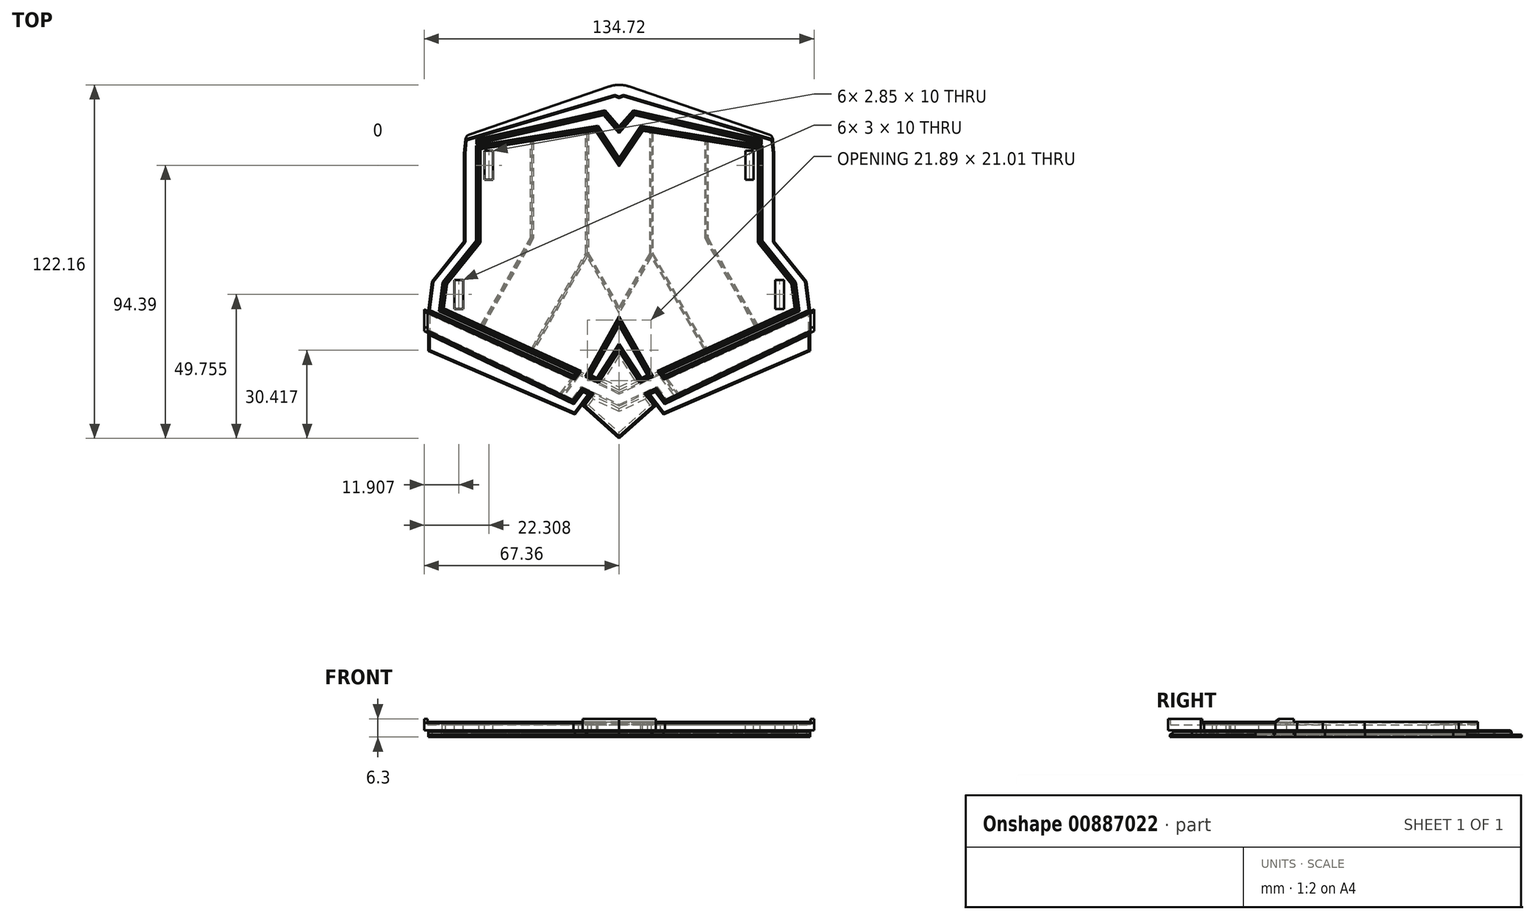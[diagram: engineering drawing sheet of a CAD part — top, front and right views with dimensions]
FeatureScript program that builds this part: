
annotation { "Feature Type Name" : "Feature", "Feature Type Description" : "" }
export const myFeature = defineFeature(function(context is Context, id is Id, definition is map)
    precondition{}
    {
        {
            var Q0;
            Q0=qCreatedBy(makeId("Top.planeOp"),FACE);
            var sketch = newSketch(context, id + "F0", { "sketchPlane" : qUnion([Q0])});
            skLineSegment(sketch, "E0", {"start": v(0, 68.56) * mm, "end": v(1.41, 69.18) * mm});
            skLineSegment(sketch, "E1", {"start": v(1.41, 69.18) * mm, "end": v(53.17, 53.82) * mm});
            skLineSegment(sketch, "E2", {"start": v(53.17, 53.82) * mm, "end": v(53.6, 49) * mm});
            skLineSegment(sketch, "E3", {"start": v(53.6, 49) * mm, "end": v(53.6, 18.48) * mm});
            skLineSegment(sketch, "E4", {"start": v(53.6, 18.48) * mm, "end": v(64.65, 4.74) * mm});
            skLineSegment(sketch, "E5", {"start": v(64.65, 4.74) * mm, "end": v(65.96, -5.54) * mm});
            skLineSegment(sketch, "E6", {"start": v(65.96, -5.54) * mm, "end": v(65.96, -19.34) * mm});
            skLineSegment(sketch, "E7", {"start": v(65.96, -19.34) * mm, "end": v(15.29, -41.25) * mm});
            skLineSegment(sketch, "E8", {"start": v(15.29, -41.25) * mm, "end": v(12.57, -37.67) * mm});
            skLineSegment(sketch, "E9", {"start": v(12.57, -37.67) * mm, "end": v(0, -48.86) * mm});
            skLineSegment(sketch, "E10.MirrorCS", {"start": v(-15.29, -41.25) * mm, "end": v(-12.57, -37.67) * mm});
            skLineSegment(sketch, "E11.MirrorCS", {"start": v(0, 68.56) * mm, "end": v(-1.41, 69.18) * mm});
            skLineSegment(sketch, "E12.MirrorCS", {"start": v(-53.6, 18.48) * mm, "end": v(-64.65, 4.74) * mm});
            skLineSegment(sketch, "E13.MirrorCS", {"start": v(-65.96, -5.54) * mm, "end": v(-65.96, -19.34) * mm});
            skLineSegment(sketch, "E14.MirrorCS", {"start": v(-65.96, -19.34) * mm, "end": v(-15.29, -41.25) * mm});
            skLineSegment(sketch, "E15.MirrorCS", {"start": v(-53.17, 53.82) * mm, "end": v(-53.6, 49) * mm});
            skLineSegment(sketch, "E16.MirrorCS", {"start": v(-1.41, 69.18) * mm, "end": v(-53.17, 53.82) * mm});
            skLineSegment(sketch, "E17.MirrorCS", {"start": v(-53.6, 49) * mm, "end": v(-53.6, 18.48) * mm});
            skLineSegment(sketch, "E18.MirrorCS", {"start": v(-12.57, -37.67) * mm, "end": v(0, -48.86) * mm});
            skLineSegment(sketch, "E19.MirrorCS", {"start": v(-64.65, 4.74) * mm, "end": v(-65.96, -5.54) * mm});
            skLineSegment(sketch, "E20", {"start": v(3.44, 72.1) * mm, "end": v(51.78, 55.53) * mm});
            skArc(sketch, "E21", {"start": v(53.17, 53.82) * mm, "mid": v(52.72, 54.88) * mm, "end": v(51.78, 55.53) * mm});
            skArc(sketch, "E22", {"start": v(3.44, 72.1) * mm, "mid": v(1.75, 72.52) * mm, "end": v(0, 72.62) * mm});
            skArc(sketch, "E23.MirrorCS", {"start": v(-3.44, 72.1) * mm, "mid": v(-1.75, 72.52) * mm, "end": v(0, 72.62) * mm});
            skLineSegment(sketch, "E24.MirrorCS", {"start": v(-3.44, 72.1) * mm, "end": v(-51.78, 55.53) * mm});
            skArc(sketch, "E25.MirrorCS", {"start": v(-53.17, 53.82) * mm, "mid": v(-52.72, 54.88) * mm, "end": v(-51.78, 55.53) * mm});
            skSolve(sketch);
        }
        {
            var Q0;
            Q0 = qSketchRegion(id + "F0", true);
            extrude(context, id + "F1", {"entities" : qUnion([Q0]), "depth" : .8 * mm, "offsetDistance" : 25 * mm});
        }
        {
            var Q0;
            Q0=makeQuery(id+"F1.opExtrude","CAP_FACE",FACE,{"disambiguationData":[OSD([sQuery(id+"F0.wireOp",EDGE,"E2"),sQuery(id+"F0.wireOp",EDGE,"E3"),sQuery(id+"F0.wireOp",EDGE,"E4"),sQuery(id+"F0.wireOp",EDGE,"E5"),sQuery(id+"F0.wireOp",EDGE,"E6"),sQuery(id+"F0.wireOp",EDGE,"E7"),sQuery(id+"F0.wireOp",EDGE,"E8"),sQuery(id+"F0.wireOp",EDGE,"E9"),sQuery(id+"F0.wireOp",EDGE,"E10.MirrorCS"),sQuery(id+"F0.wireOp",EDGE,"E12.MirrorCS"),sQuery(id+"F0.wireOp",EDGE,"E13.MirrorCS"),sQuery(id+"F0.wireOp",EDGE,"E14.MirrorCS"),sQuery(id+"F0.wireOp",EDGE,"E15.MirrorCS"),sQuery(id+"F0.wireOp",EDGE,"E17.MirrorCS"),sQuery(id+"F0.wireOp",EDGE,"E18.MirrorCS"),sQuery(id+"F0.wireOp",EDGE,"E19.MirrorCS"),sQuery(id+"F0.wireOp",EDGE,"E20"),sQuery(id+"F0.wireOp",EDGE,"E21"),sQuery(id+"F0.wireOp",EDGE,"E22"),sQuery(id+"F0.wireOp",EDGE,"E23.MirrorCS"),sQuery(id+"F0.wireOp",EDGE,"E24.MirrorCS"),sQuery(id+"F0.wireOp",EDGE,"E25.MirrorCS")])],"isStart":false});
            var sketch = newSketch(context, id + "F2", { "sketchPlane" : qUnion([Q0])});
            skLineSegment(sketch, "E26", {"start": v(48.77, 53.39) * mm, "end": v(48.77, 18.48) * mm});
            skLineSegment(sketch, "E27", {"start": v(48.77, 18.48) * mm, "end": v(60.35, 4.1) * mm});
            skLineSegment(sketch, "E28", {"start": v(60.35, 4.1) * mm, "end": v(61.53, -5.14) * mm});
            skLineSegment(sketch, "E29", {"start": v(61.53, -5.14) * mm, "end": v(14.26, -26.68) * mm});
            skLineSegment(sketch, "E30", {"start": v(65.96, -5.54) * mm, "end": v(15.61, -28.48) * mm});
            skLineSegment(sketch, "E31", {"start": v(15.61, -28.48) * mm, "end": v(14.26, -26.68) * mm});
            skLineSegment(sketch, "E32", {"start": v(53.6, 49) * mm, "end": v(53.17, 53.82) * mm});
            skLineSegment(sketch, "E33", {"start": v(53.17, 53.82) * mm, "end": v(1.41, 69.18) * mm});
            skLineSegment(sketch, "E34", {"start": v(1.41, 69.18) * mm, "end": v(0, 68.56) * mm});
            skLineSegment(sketch, "E35", {"start": v(0, 57.52) * mm, "end": v(5.09, 63.36) * mm});
            skLineSegment(sketch, "E36", {"start": v(5.09, 63.36) * mm, "end": v(48.77, 53.39) * mm});
            skLineSegment(sketch, "E37", {"start": v(53.6, 49) * mm, "end": v(53.6, 18.48) * mm});
            skLineSegment(sketch, "E38", {"start": v(53.6, 18.48) * mm, "end": v(64.65, 4.74) * mm});
            skLineSegment(sketch, "E39", {"start": v(64.65, 4.74) * mm, "end": v(65.96, -5.54) * mm});
            skLineSegment(sketch, "E40.MirrorCS", {"start": v(-15.61, -28.48) * mm, "end": v(-14.26, -26.68) * mm});
            skLineSegment(sketch, "E41.MirrorCS", {"start": v(-1.41, 69.18) * mm, "end": v(0, 68.56) * mm});
            skLineSegment(sketch, "E42.MirrorCS", {"start": v(-60.35, 4.1) * mm, "end": v(-61.53, -5.14) * mm});
            skLineSegment(sketch, "E43.MirrorCS", {"start": v(-61.53, -5.14) * mm, "end": v(-14.26, -26.68) * mm});
            skLineSegment(sketch, "E44.MirrorCS", {"start": v(-64.65, 4.74) * mm, "end": v(-65.96, -5.54) * mm});
            skLineSegment(sketch, "E45.MirrorCS", {"start": v(-53.6, 49) * mm, "end": v(-53.17, 53.82) * mm});
            skLineSegment(sketch, "E46.MirrorCS", {"start": v(0, 57.52) * mm, "end": v(-5.09, 63.36) * mm});
            skLineSegment(sketch, "E47.MirrorCS", {"start": v(-53.6, 18.48) * mm, "end": v(-64.65, 4.74) * mm});
            skLineSegment(sketch, "E48.MirrorCS", {"start": v(-48.77, 53.39) * mm, "end": v(-48.77, 18.48) * mm});
            skLineSegment(sketch, "E49.MirrorCS", {"start": v(-53.6, 49) * mm, "end": v(-53.6, 18.48) * mm});
            skLineSegment(sketch, "E50.MirrorCS", {"start": v(-53.17, 53.82) * mm, "end": v(-1.41, 69.18) * mm});
            skLineSegment(sketch, "E51.MirrorCS", {"start": v(-5.09, 63.36) * mm, "end": v(-48.77, 53.39) * mm});
            skLineSegment(sketch, "E52.MirrorCS", {"start": v(-65.96, -5.54) * mm, "end": v(-15.61, -28.48) * mm});
            skLineSegment(sketch, "E53.MirrorCS", {"start": v(-48.77, 18.48) * mm, "end": v(-60.35, 4.1) * mm});
            skSolve(sketch);
        }
        {
            var Q0;
            Q0=qSketchRegion(id+"F2",true);
            extrude(context, id + "F3", {"entities" : qUnion([Q0]), "operationType" : NewBodyOperationType.ADD, "depth" : 1.5 * mm, "offsetDistance" : 25 * mm});
        }
        {
            var Q0;
            {var subQ0=sQuery(id+"F0.wireOp",EDGE,"E8");var subQ1=sQuery(id+"F0.wireOp",EDGE,"E7");var subQ2=sQuery(id+"F0.wireOp",EDGE,"E6");var subQ3=sQuery(id+"F0.wireOp",EDGE,"E19.MirrorCS");var subQ4=sQuery(id+"F0.wireOp",EDGE,"E5");var subQ5=sQuery(id+"F0.wireOp",EDGE,"E18.MirrorCS");var subQ6=sQuery(id+"F0.wireOp",EDGE,"E9");var subQ7=sQuery(id+"F0.wireOp",EDGE,"E10.MirrorCS");var subQ8=sQuery(id+"F0.wireOp",EDGE,"E13.MirrorCS");var subQ9=sQuery(id+"F0.wireOp",EDGE,"E14.MirrorCS");Q0=makeQuery(id+"F3.boolean.opBoolean","SPLIT",FACE,{"disambiguationData":[TD([makeQuery(id+"F1.opExtrude","SWEPT_FACE",FACE,{"disambiguationData":[OSD([subQ4])]})])],"derivedFrom":makeQuery(id+"F1.opExtrude","CAP_FACE",FACE,{"disambiguationData":[OSD([sQuery(id+"F0.wireOp",EDGE,"E2"),sQuery(id+"F0.wireOp",EDGE,"E3"),sQuery(id+"F0.wireOp",EDGE,"E4"),subQ4,subQ2,subQ1,subQ0,subQ6,subQ7,sQuery(id+"F0.wireOp",EDGE,"E12.MirrorCS"),subQ8,subQ9,sQuery(id+"F0.wireOp",EDGE,"E15.MirrorCS"),sQuery(id+"F0.wireOp",EDGE,"E17.MirrorCS"),subQ5,subQ3,sQuery(id+"F0.wireOp",EDGE,"E20"),sQuery(id+"F0.wireOp",EDGE,"E21"),sQuery(id+"F0.wireOp",EDGE,"E22"),sQuery(id+"F0.wireOp",EDGE,"E23.MirrorCS"),sQuery(id+"F0.wireOp",EDGE,"E24.MirrorCS"),sQuery(id+"F0.wireOp",EDGE,"E25.MirrorCS")])],"isStart":false})});}
            var sketch = newSketch(context, id + "F4", { "sketchPlane" : qUnion([Q0])});
            skLineSegment(sketch, "E54", {"start": v(0, 56.8) * mm, "end": v(5.24, 62.81) * mm});
            skLineSegment(sketch, "E55", {"start": v(5.24, 62.81) * mm, "end": v(48.77, 52.87) * mm});
            skLineSegment(sketch, "E56", {"start": v(48.77, 52.87) * mm, "end": v(48.77, 51.1) * mm});
            skLineSegment(sketch, "E57", {"start": v(48.77, 51.1) * mm, "end": v(7.78, 57.76) * mm});
            skLineSegment(sketch, "E58", {"start": v(7.78, 57.76) * mm, "end": v(0, 46.14) * mm});
            skLineSegment(sketch, "E59.MirrorCS", {"start": v(-48.77, 52.87) * mm, "end": v(-48.77, 51.1) * mm});
            skLineSegment(sketch, "E60.MirrorCS", {"start": v(-48.77, 51.1) * mm, "end": v(-7.78, 57.76) * mm});
            skLineSegment(sketch, "E61.MirrorCS", {"start": v(-5.24, 62.81) * mm, "end": v(-48.77, 52.87) * mm});
            skLineSegment(sketch, "E62.MirrorCS", {"start": v(0, 56.8) * mm, "end": v(-5.24, 62.81) * mm});
            skLineSegment(sketch, "E63.MirrorCS", {"start": v(-7.78, 57.76) * mm, "end": v(0, 46.14) * mm});
            skSolve(sketch);
        }
        {
            var Q0;
            Q0=qSketchRegion(id+"F4",true);
            extrude(context, id + "F5", {"entities" : qUnion([Q0]), "operationType" : NewBodyOperationType.ADD, "depth" : 1.5 * mm, "offsetDistance" : 25 * mm});
        }
        {
            var Q0;
            {var subQ7=sQuery(id+"F0.wireOp",EDGE,"E8");var subQ9=sQuery(id+"F0.wireOp",EDGE,"E7");var subQ11=sQuery(id+"F0.wireOp",EDGE,"E6");var subQ14=sQuery(id+"F0.wireOp",EDGE,"E19.MirrorCS");var subQ16=sQuery(id+"F0.wireOp",EDGE,"E5");var subQ17=makeQuery(id+"F1.opExtrude","SWEPT_FACE",FACE,{"disambiguationData":[OSD([subQ16])]});var subQ19=sQuery(id+"F0.wireOp",EDGE,"E18.MirrorCS");var subQ22=sQuery(id+"F0.wireOp",EDGE,"E9");var subQ24=sQuery(id+"F0.wireOp",EDGE,"E10.MirrorCS");var subQ27=sQuery(id+"F0.wireOp",EDGE,"E13.MirrorCS");var subQ30=sQuery(id+"F0.wireOp",EDGE,"E14.MirrorCS");Q0=makeQuery(id+"F5.boolean.opBoolean","SPLIT",FACE,{"disambiguationData":[TD([subQ17])],"derivedFrom":makeQuery(id+"F3.boolean.opBoolean","SPLIT",FACE,{"disambiguationData":[TD([subQ17])],"derivedFrom":makeQuery(id+"F1.opExtrude","CAP_FACE",FACE,{"disambiguationData":[OSD([sQuery(id+"F0.wireOp",EDGE,"E2"),sQuery(id+"F0.wireOp",EDGE,"E3"),sQuery(id+"F0.wireOp",EDGE,"E4"),subQ16,subQ11,subQ9,subQ7,subQ22,subQ24,sQuery(id+"F0.wireOp",EDGE,"E12.MirrorCS"),subQ27,subQ30,sQuery(id+"F0.wireOp",EDGE,"E15.MirrorCS"),sQuery(id+"F0.wireOp",EDGE,"E17.MirrorCS"),subQ19,subQ14,sQuery(id+"F0.wireOp",EDGE,"E20"),sQuery(id+"F0.wireOp",EDGE,"E21"),sQuery(id+"F0.wireOp",EDGE,"E22"),sQuery(id+"F0.wireOp",EDGE,"E23.MirrorCS"),sQuery(id+"F0.wireOp",EDGE,"E24.MirrorCS"),sQuery(id+"F0.wireOp",EDGE,"E25.MirrorCS")])],"isStart":false})})});}
            var sketch = newSketch(context, id + "F6", { "sketchPlane" : qUnion([Q0])});
            skLineSegment(sketch, "E64", {"start": v(0, -9.12) * mm, "end": v(10.6, -27.8) * mm});
            skLineSegment(sketch, "E65", {"start": v(10.6, -27.8) * mm, "end": v(7.46, -29.31) * mm});
            skLineSegment(sketch, "E66", {"start": v(7.46, -29.31) * mm, "end": v(0, -17.78) * mm});
            skLineSegment(sketch, "E67", {"start": v(12.66, -32.86) * mm, "end": v(9.9, -34.17) * mm});
            skLineSegment(sketch, "E68", {"start": v(9.9, -34.17) * mm, "end": v(15.28, -41.22) * mm});
            skLineSegment(sketch, "E69", {"start": v(15.28, -41.22) * mm, "end": v(65.96, -19.32) * mm});
            skLineSegment(sketch, "E70", {"start": v(65.96, -19.32) * mm, "end": v(65.96, -13.1) * mm});
            skLineSegment(sketch, "E71", {"start": v(65.96, -13.1) * mm, "end": v(15.81, -37.08) * mm});
            skLineSegment(sketch, "E72", {"start": v(15.81, -37.08) * mm, "end": v(12.66, -32.86) * mm});
            skLineSegment(sketch, "E73.MirrorCS", {"start": v(-12.66, -32.86) * mm, "end": v(-9.9, -34.17) * mm});
            skLineSegment(sketch, "E74.MirrorCS", {"start": v(-15.81, -37.08) * mm, "end": v(-12.66, -32.86) * mm});
            skLineSegment(sketch, "E75.MirrorCS", {"start": v(-10.6, -27.8) * mm, "end": v(-7.46, -29.31) * mm});
            skLineSegment(sketch, "E76.MirrorCS", {"start": v(-65.96, -19.32) * mm, "end": v(-65.96, -13.1) * mm});
            skLineSegment(sketch, "E77.MirrorCS", {"start": v(-65.96, -13.1) * mm, "end": v(-15.81, -37.08) * mm});
            skLineSegment(sketch, "E78.MirrorCS", {"start": v(-9.9, -34.17) * mm, "end": v(-15.28, -41.22) * mm});
            skLineSegment(sketch, "E79.MirrorCS", {"start": v(-15.28, -41.22) * mm, "end": v(-65.96, -19.32) * mm});
            skLineSegment(sketch, "E80.MirrorCS", {"start": v(-7.46, -29.31) * mm, "end": v(0, -17.78) * mm});
            skLineSegment(sketch, "E81.MirrorCS", {"start": v(0, -9.12) * mm, "end": v(-10.6, -27.8) * mm});
            skSolve(sketch);
        }
        {
            var Q0;
            Q0=qSketchRegion(id+"F6",true);
            extrude(context, id + "F7", {"entities" : qUnion([Q0]), "operationType" : NewBodyOperationType.ADD, "depth" : 1.5 * mm, "offsetDistance" : 25 * mm});
        }
        {
            var Q0;
            {var subQ7=sQuery(id+"F0.wireOp",EDGE,"E8");var subQ9=sQuery(id+"F0.wireOp",EDGE,"E7");var subQ11=sQuery(id+"F0.wireOp",EDGE,"E6");var subQ14=sQuery(id+"F0.wireOp",EDGE,"E19.MirrorCS");var subQ16=sQuery(id+"F0.wireOp",EDGE,"E5");var subQ17=makeQuery(id+"F1.opExtrude","SWEPT_FACE",FACE,{"disambiguationData":[OSD([subQ16])]});var subQ19=sQuery(id+"F0.wireOp",EDGE,"E18.MirrorCS");var subQ22=sQuery(id+"F0.wireOp",EDGE,"E9");var subQ24=sQuery(id+"F0.wireOp",EDGE,"E10.MirrorCS");var subQ27=sQuery(id+"F0.wireOp",EDGE,"E13.MirrorCS");var subQ30=sQuery(id+"F0.wireOp",EDGE,"E14.MirrorCS");Q0=makeQuery(id+"F5.boolean.opBoolean","SPLIT",FACE,{"disambiguationData":[TD([subQ17])],"derivedFrom":makeQuery(id+"F3.boolean.opBoolean","SPLIT",FACE,{"disambiguationData":[TD([subQ17])],"derivedFrom":makeQuery(id+"F1.opExtrude","CAP_FACE",FACE,{"disambiguationData":[OSD([sQuery(id+"F0.wireOp",EDGE,"E2"),sQuery(id+"F0.wireOp",EDGE,"E3"),sQuery(id+"F0.wireOp",EDGE,"E4"),subQ16,subQ11,subQ9,subQ7,subQ22,subQ24,sQuery(id+"F0.wireOp",EDGE,"E12.MirrorCS"),subQ27,subQ30,sQuery(id+"F0.wireOp",EDGE,"E15.MirrorCS"),sQuery(id+"F0.wireOp",EDGE,"E17.MirrorCS"),subQ19,subQ14,sQuery(id+"F0.wireOp",EDGE,"E20"),sQuery(id+"F0.wireOp",EDGE,"E21"),sQuery(id+"F0.wireOp",EDGE,"E22"),sQuery(id+"F0.wireOp",EDGE,"E23.MirrorCS"),sQuery(id+"F0.wireOp",EDGE,"E24.MirrorCS"),sQuery(id+"F0.wireOp",EDGE,"E25.MirrorCS")])],"isStart":false})})});}
            var sketch = newSketch(context, id + "F8", { "sketchPlane" : qUnion([Q0])});
            skLineSegment(sketch, "E82", {"start": v(65.96, -6.1) * mm, "end": v(15.92, -28.9) * mm});
            skLineSegment(sketch, "E83", {"start": v(15.92, -28.9) * mm, "end": v(20.1, -34.47) * mm});
            skLineSegment(sketch, "E84", {"start": v(20.1, -34.47) * mm, "end": v(65.96, -12.55) * mm});
            skLineSegment(sketch, "E85", {"start": v(65.96, -12.55) * mm, "end": v(65.96, -6.1) * mm});
            skLineSegment(sketch, "E86.MirrorCS", {"start": v(-15.92, -28.9) * mm, "end": v(-20.1, -34.47) * mm});
            skLineSegment(sketch, "E87.MirrorCS", {"start": v(-65.96, -12.55) * mm, "end": v(-65.96, -6.1) * mm});
            skLineSegment(sketch, "E88.MirrorCS", {"start": v(-65.96, -6.1) * mm, "end": v(-15.92, -28.9) * mm});
            skLineSegment(sketch, "E89.MirrorCS", {"start": v(-20.1, -34.47) * mm, "end": v(-65.96, -12.55) * mm});
            skSolve(sketch);
        }
        {
            var Q0;
            Q0=qSketchRegion(id+"F8",true);
            extrude(context, id + "F9", {"entities" : qUnion([Q0]), "operationType" : NewBodyOperationType.ADD, "depth" : 1.5 * mm, "offsetDistance" : 25 * mm});
        }
        {
            var Q0;
            {var subQ7=sQuery(id+"F0.wireOp",EDGE,"E8");var subQ9=sQuery(id+"F0.wireOp",EDGE,"E7");var subQ11=sQuery(id+"F0.wireOp",EDGE,"E6");var subQ14=sQuery(id+"F0.wireOp",EDGE,"E19.MirrorCS");var subQ16=sQuery(id+"F0.wireOp",EDGE,"E5");var subQ17=makeQuery(id+"F1.opExtrude","SWEPT_FACE",FACE,{"disambiguationData":[OSD([subQ16])]});var subQ19=sQuery(id+"F0.wireOp",EDGE,"E18.MirrorCS");var subQ22=sQuery(id+"F0.wireOp",EDGE,"E9");var subQ24=sQuery(id+"F0.wireOp",EDGE,"E10.MirrorCS");var subQ27=sQuery(id+"F0.wireOp",EDGE,"E13.MirrorCS");var subQ30=sQuery(id+"F0.wireOp",EDGE,"E14.MirrorCS");Q0=makeQuery(id+"F5.boolean.opBoolean","SPLIT",FACE,{"disambiguationData":[TD([subQ17])],"derivedFrom":makeQuery(id+"F3.boolean.opBoolean","SPLIT",FACE,{"disambiguationData":[TD([subQ17])],"derivedFrom":makeQuery(id+"F1.opExtrude","CAP_FACE",FACE,{"disambiguationData":[OSD([sQuery(id+"F0.wireOp",EDGE,"E2"),sQuery(id+"F0.wireOp",EDGE,"E3"),sQuery(id+"F0.wireOp",EDGE,"E4"),subQ16,subQ11,subQ9,subQ7,subQ22,subQ24,sQuery(id+"F0.wireOp",EDGE,"E12.MirrorCS"),subQ27,subQ30,sQuery(id+"F0.wireOp",EDGE,"E15.MirrorCS"),sQuery(id+"F0.wireOp",EDGE,"E17.MirrorCS"),subQ19,subQ14,sQuery(id+"F0.wireOp",EDGE,"E20"),sQuery(id+"F0.wireOp",EDGE,"E21"),sQuery(id+"F0.wireOp",EDGE,"E22"),sQuery(id+"F0.wireOp",EDGE,"E23.MirrorCS"),sQuery(id+"F0.wireOp",EDGE,"E24.MirrorCS"),sQuery(id+"F0.wireOp",EDGE,"E25.MirrorCS")])],"isStart":false})})});}
            var sketch = newSketch(context, id + "F10", { "sketchPlane" : qUnion([Q0])});
            skLineSegment(sketch, "E90", {"start": v(0, -38.38) * mm, "end": v(12.83, -32.26) * mm});
            skLineSegment(sketch, "E91", {"start": v(0, -33.68) * mm, "end": v(13.91, -27.04) * mm});
            skLineSegment(sketch, "E92", {"start": v(13.91, -27.04) * mm, "end": v(19.6, -34.65) * mm});
            skLineSegment(sketch, "E93", {"start": v(12.83, -32.26) * mm, "end": v(16.08, -36.6) * mm});
            skLineSegment(sketch, "E94", {"start": v(16.08, -36.6) * mm, "end": v(19.6, -34.65) * mm});
            skLineSegment(sketch, "E95.MirrorCS", {"start": v(-12.83, -32.26) * mm, "end": v(-16.08, -36.6) * mm});
            skLineSegment(sketch, "E96.MirrorCS", {"start": v(-16.08, -36.6) * mm, "end": v(-19.6, -34.65) * mm});
            skLineSegment(sketch, "E97.MirrorCS", {"start": v(0, -33.68) * mm, "end": v(-13.91, -27.04) * mm});
            skLineSegment(sketch, "E98.MirrorCS", {"start": v(-13.91, -27.04) * mm, "end": v(-19.6, -34.65) * mm});
            skLineSegment(sketch, "E99.MirrorCS", {"start": v(0, -38.38) * mm, "end": v(-12.83, -32.26) * mm});
            skSolve(sketch);
        }
        {
            var Q0;
            Q0=qSketchRegion(id+"F10",true);
            extrude(context, id + "F11", {"entities" : qUnion([Q0]), "operationType" : NewBodyOperationType.ADD, "depth" : 1.5 * mm, "offsetDistance" : 25 * mm});
        }
        {
            var Q0;
            {var subQ7=sQuery(id+"F0.wireOp",EDGE,"E8");var subQ9=sQuery(id+"F0.wireOp",EDGE,"E7");var subQ11=sQuery(id+"F0.wireOp",EDGE,"E6");var subQ14=sQuery(id+"F0.wireOp",EDGE,"E19.MirrorCS");var subQ16=sQuery(id+"F0.wireOp",EDGE,"E5");var subQ17=makeQuery(id+"F1.opExtrude","SWEPT_FACE",FACE,{"disambiguationData":[OSD([subQ16])]});var subQ19=sQuery(id+"F0.wireOp",EDGE,"E18.MirrorCS");var subQ22=sQuery(id+"F0.wireOp",EDGE,"E9");var subQ24=sQuery(id+"F0.wireOp",EDGE,"E10.MirrorCS");var subQ27=sQuery(id+"F0.wireOp",EDGE,"E13.MirrorCS");var subQ30=sQuery(id+"F0.wireOp",EDGE,"E14.MirrorCS");Q0=makeQuery(id+"F5.boolean.opBoolean","SPLIT",FACE,{"disambiguationData":[TD([subQ17])],"derivedFrom":makeQuery(id+"F3.boolean.opBoolean","SPLIT",FACE,{"disambiguationData":[TD([subQ17])],"derivedFrom":makeQuery(id+"F1.opExtrude","CAP_FACE",FACE,{"disambiguationData":[OSD([sQuery(id+"F0.wireOp",EDGE,"E2"),sQuery(id+"F0.wireOp",EDGE,"E3"),sQuery(id+"F0.wireOp",EDGE,"E4"),subQ16,subQ11,subQ9,subQ7,subQ22,subQ24,sQuery(id+"F0.wireOp",EDGE,"E12.MirrorCS"),subQ27,subQ30,sQuery(id+"F0.wireOp",EDGE,"E15.MirrorCS"),sQuery(id+"F0.wireOp",EDGE,"E17.MirrorCS"),subQ19,subQ14,sQuery(id+"F0.wireOp",EDGE,"E20"),sQuery(id+"F0.wireOp",EDGE,"E21"),sQuery(id+"F0.wireOp",EDGE,"E22"),sQuery(id+"F0.wireOp",EDGE,"E23.MirrorCS"),sQuery(id+"F0.wireOp",EDGE,"E24.MirrorCS"),sQuery(id+"F0.wireOp",EDGE,"E25.MirrorCS")])],"isStart":false})})});}
            var sketch = newSketch(context, id + "F12", { "sketchPlane" : qUnion([Q0])});
            skLineSegment(sketch, "E100", {"start": v(0, -32.85) * mm, "end": v(6.76, -29.62) * mm});
            skLineSegment(sketch, "E101", {"start": v(6.76, -29.62) * mm, "end": v(0, -19.16) * mm});
            skLineSegment(sketch, "E102", {"start": v(0, -39.2) * mm, "end": v(9.4, -34.73) * mm});
            skLineSegment(sketch, "E103", {"start": v(9.4, -34.73) * mm, "end": v(12.01, -38.16) * mm});
            skLineSegment(sketch, "E104", {"start": v(12.01, -38.16) * mm, "end": v(0, -48.86) * mm});
            skLineSegment(sketch, "E105.MirrorCS", {"start": v(-12.01, -38.16) * mm, "end": v(0, -48.86) * mm});
            skLineSegment(sketch, "E106.MirrorCS", {"start": v(-9.4, -34.73) * mm, "end": v(-12.01, -38.16) * mm});
            skLineSegment(sketch, "E107.MirrorCS", {"start": v(-6.76, -29.62) * mm, "end": v(0, -19.16) * mm});
            skLineSegment(sketch, "E108.MirrorCS", {"start": v(0, -39.2) * mm, "end": v(-9.4, -34.73) * mm});
            skLineSegment(sketch, "E109.MirrorCS", {"start": v(0, -32.85) * mm, "end": v(-6.76, -29.62) * mm});
            skSolve(sketch);
        }
        {
            var Q0;
            Q0=qSketchRegion(id+"F12",true);
            extrude(context, id + "F13", {"entities" : qUnion([Q0]), "operationType" : NewBodyOperationType.ADD, "depth" : 1 * mm, "offsetDistance" : 25 * mm});
        }
        {
            var Q0;
            Q0=makeQuery(id+"F11.opExtrude","CAP_FACE",FACE,{"disambiguationData":[OSD([sQuery(id+"F10.wireOp",EDGE,"E90"),sQuery(id+"F10.wireOp",EDGE,"E91"),sQuery(id+"F10.wireOp",EDGE,"E92"),sQuery(id+"F10.wireOp",EDGE,"E93"),sQuery(id+"F10.wireOp",EDGE,"E94"),sQuery(id+"F10.wireOp",EDGE,"E95.MirrorCS"),sQuery(id+"F10.wireOp",EDGE,"E96.MirrorCS"),sQuery(id+"F10.wireOp",EDGE,"E97.MirrorCS"),sQuery(id+"F10.wireOp",EDGE,"E98.MirrorCS"),sQuery(id+"F10.wireOp",EDGE,"E99.MirrorCS")])],"isStart":false});
            var sketch = newSketch(context, id + "F14", { "sketchPlane" : qUnion([Q0])});
            skLineSegment(sketch, "E110", {"start": v(67.36, -4.9) * mm, "end": v(67.36, -12.43) * mm});
            skLineSegment(sketch, "E111", {"start": v(12.69, -38.23) * mm, "end": v(0, -49.53) * mm});
            skLineSegment(sketch, "E112", {"start": v(12.69, -38.23) * mm, "end": v(9.7, -34.3) * mm});
            skLineSegment(sketch, "E113", {"start": v(9.7, -34.3) * mm, "end": v(12.68, -32.89) * mm});
            skLineSegment(sketch, "E114", {"start": v(12.68, -32.89) * mm, "end": v(15.81, -37.08) * mm});
            skLineSegment(sketch, "E115", {"start": v(0, -18.24) * mm, "end": v(7.36, -29.62) * mm});
            skLineSegment(sketch, "E116", {"start": v(7.36, -29.62) * mm, "end": v(14.07, -26.42) * mm});
            skLineSegment(sketch, "E117", {"start": v(14.07, -26.42) * mm, "end": v(15.61, -28.48) * mm});
            skLineSegment(sketch, "E118", {"start": v(15.61, -28.48) * mm, "end": v(67.36, -4.9) * mm});
            skLineSegment(sketch, "E119", {"start": v(15.81, -37.08) * mm, "end": v(67.36, -12.43) * mm});
            skLineSegment(sketch, "E120", {"start": v(14.1, -26.48) * mm, "end": v(61.26, -5) * mm});
            skLineSegment(sketch, "E121", {"start": v(61.26, -5) * mm, "end": v(60.1, 4) * mm});
            skLineSegment(sketch, "E122", {"start": v(60.1, 4) * mm, "end": v(48.52, 18.4) * mm});
            skLineSegment(sketch, "E123", {"start": v(48.52, 18.4) * mm, "end": v(48.52, 50.9) * mm});
            skLineSegment(sketch, "E124", {"start": v(48.52, 50.9) * mm, "end": v(7.9, 57.48) * mm});
            skLineSegment(sketch, "E125", {"start": v(7.9, 57.48) * mm, "end": v(0, 45.69) * mm});
            skLineSegment(sketch, "E126", {"start": v(10.95, -27.9) * mm, "end": v(0, -8.6) * mm});
            skLineSegment(sketch, "E127.MirrorCS", {"start": v(-9.7, -34.3) * mm, "end": v(-12.68, -32.89) * mm});
            skLineSegment(sketch, "E128.MirrorCS", {"start": v(-12.69, -38.23) * mm, "end": v(-9.7, -34.3) * mm});
            skLineSegment(sketch, "E129.MirrorCS", {"start": v(-12.68, -32.89) * mm, "end": v(-15.81, -37.08) * mm});
            skLineSegment(sketch, "E130.MirrorCS", {"start": v(-14.07, -26.42) * mm, "end": v(-15.61, -28.48) * mm});
            skLineSegment(sketch, "E131.MirrorCS", {"start": v(-67.36, -4.9) * mm, "end": v(-67.36, -12.43) * mm});
            skLineSegment(sketch, "E132.MirrorCS", {"start": v(-7.36, -29.62) * mm, "end": v(-14.07, -26.42) * mm});
            skLineSegment(sketch, "E133.MirrorCS", {"start": v(-14.1, -26.48) * mm, "end": v(-61.26, -5) * mm});
            skLineSegment(sketch, "E134.MirrorCS", {"start": v(-12.69, -38.23) * mm, "end": v(0, -49.53) * mm});
            skLineSegment(sketch, "E135.MirrorCS", {"start": v(-48.52, 18.4) * mm, "end": v(-48.52, 50.9) * mm});
            skLineSegment(sketch, "E136.MirrorCS", {"start": v(-60.1, 4) * mm, "end": v(-48.52, 18.4) * mm});
            skLineSegment(sketch, "E137.MirrorCS", {"start": v(-10.95, -27.9) * mm, "end": v(0, -8.6) * mm});
            skLineSegment(sketch, "E138.MirrorCS", {"start": v(-48.52, 50.9) * mm, "end": v(-7.9, 57.48) * mm});
            skLineSegment(sketch, "E139.MirrorCS", {"start": v(-15.81, -37.08) * mm, "end": v(-67.36, -12.43) * mm});
            skLineSegment(sketch, "E140.MirrorCS", {"start": v(-15.61, -28.48) * mm, "end": v(-67.36, -4.9) * mm});
            skLineSegment(sketch, "E141.MirrorCS", {"start": v(0, -18.24) * mm, "end": v(-7.36, -29.62) * mm});
            skLineSegment(sketch, "E142.MirrorCS", {"start": v(-61.26, -5) * mm, "end": v(-60.1, 4) * mm});
            skLineSegment(sketch, "E143.MirrorCS", {"start": v(-7.9, 57.48) * mm, "end": v(0, 45.69) * mm});
            skSolve(sketch);
        }
        {
            var Q0;
            Q0 = qSketchRegion(id + "F14", true);
            extrude(context, id + "F15", {"entities" : qUnion([Q0]), "depth" : 2 * mm, "offsetDistance" : 25 * mm});
        }
        {
            var Q0;
            Q0=makeQuery(id+"F1.opExtrude","CAP_FACE",FACE,{"disambiguationData":[OSD([sQuery(id+"F0.wireOp",EDGE,"E2"),sQuery(id+"F0.wireOp",EDGE,"E3"),sQuery(id+"F0.wireOp",EDGE,"E4"),sQuery(id+"F0.wireOp",EDGE,"E5"),sQuery(id+"F0.wireOp",EDGE,"E6"),sQuery(id+"F0.wireOp",EDGE,"E7"),sQuery(id+"F0.wireOp",EDGE,"E8"),sQuery(id+"F0.wireOp",EDGE,"E9"),sQuery(id+"F0.wireOp",EDGE,"E10.MirrorCS"),sQuery(id+"F0.wireOp",EDGE,"E12.MirrorCS"),sQuery(id+"F0.wireOp",EDGE,"E13.MirrorCS"),sQuery(id+"F0.wireOp",EDGE,"E14.MirrorCS"),sQuery(id+"F0.wireOp",EDGE,"E15.MirrorCS"),sQuery(id+"F0.wireOp",EDGE,"E17.MirrorCS"),sQuery(id+"F0.wireOp",EDGE,"E18.MirrorCS"),sQuery(id+"F0.wireOp",EDGE,"E19.MirrorCS"),sQuery(id+"F0.wireOp",EDGE,"E20"),sQuery(id+"F0.wireOp",EDGE,"E21"),sQuery(id+"F0.wireOp",EDGE,"E22"),sQuery(id+"F0.wireOp",EDGE,"E23.MirrorCS"),sQuery(id+"F0.wireOp",EDGE,"E24.MirrorCS"),sQuery(id+"F0.wireOp",EDGE,"E25.MirrorCS")])],"isStart":false});
            var sketch = newSketch(context, id + "F16", { "sketchPlane" : qUnion([Q0])});
            skLineSegment(sketch, "E144", {"start": v(0, 45.24) * mm, "end": v(8.02, 57.21) * mm});
            skLineSegment(sketch, "E145", {"start": v(8.02, 57.21) * mm, "end": v(48.27, 50.68) * mm});
            skLineSegment(sketch, "E146", {"start": v(48.27, 50.68) * mm, "end": v(48.27, 18.3) * mm});
            skLineSegment(sketch, "E147", {"start": v(48.27, 18.3) * mm, "end": v(59.87, 3.9) * mm});
            skLineSegment(sketch, "E148", {"start": v(59.87, 3.9) * mm, "end": v(60.99, -4.84) * mm});
            skLineSegment(sketch, "E149", {"start": v(60.99, -4.84) * mm, "end": v(11.05, -27.59) * mm});
            skLineSegment(sketch, "E150", {"start": v(11.05, -27.59) * mm, "end": v(0, -8.1) * mm});
            skLineSegment(sketch, "E151.MirrorCS", {"start": v(-8.02, 57.21) * mm, "end": v(-48.27, 50.68) * mm});
            skLineSegment(sketch, "E152.MirrorCS", {"start": v(-60.99, -4.84) * mm, "end": v(-11.05, -27.59) * mm});
            skLineSegment(sketch, "E153.MirrorCS", {"start": v(-48.27, 50.68) * mm, "end": v(-48.27, 18.3) * mm});
            skLineSegment(sketch, "E154.MirrorCS", {"start": v(-11.05, -27.59) * mm, "end": v(0, -8.1) * mm});
            skLineSegment(sketch, "E155.MirrorCS", {"start": v(0, 45.24) * mm, "end": v(-8.02, 57.21) * mm});
            skLineSegment(sketch, "E156.MirrorCS", {"start": v(-59.87, 3.9) * mm, "end": v(-60.99, -4.84) * mm});
            skLineSegment(sketch, "E157.MirrorCS", {"start": v(-48.27, 18.3) * mm, "end": v(-59.87, 3.9) * mm});
            skSolve(sketch);
        }
        {
            var Q0;
            Q0=qSketchRegion(id+"F16",true);
            extrude(context, id + "F17", {"entities" : qUnion([Q0]), "depth" : .5 * mm, "offsetDistance" : 25 * mm});
        }
        {
            var Q0;
            Q0=makeQuery(id+"F17.opExtrude","CAP_FACE",FACE,{"disambiguationData":[OSD([sQuery(id+"F16.wireOp",EDGE,"E144"),sQuery(id+"F16.wireOp",EDGE,"E145"),sQuery(id+"F16.wireOp",EDGE,"E146"),sQuery(id+"F16.wireOp",EDGE,"E147"),sQuery(id+"F16.wireOp",EDGE,"E148"),sQuery(id+"F16.wireOp",EDGE,"E149"),sQuery(id+"F16.wireOp",EDGE,"E150"),sQuery(id+"F16.wireOp",EDGE,"E151.MirrorCS"),sQuery(id+"F16.wireOp",EDGE,"E152.MirrorCS"),sQuery(id+"F16.wireOp",EDGE,"E153.MirrorCS"),sQuery(id+"F16.wireOp",EDGE,"E154.MirrorCS"),sQuery(id+"F16.wireOp",EDGE,"E155.MirrorCS"),sQuery(id+"F16.wireOp",EDGE,"E156.MirrorCS"),sQuery(id+"F16.wireOp",EDGE,"E157.MirrorCS")])],"isStart":false});
            fillet(context, id + "F18", {"entities" : qUnion([Q0]), "radius" : .5 * mm, "tangentPropagation" : true, "allowEdgeOverflow" : false});
        }
        {
            var Q0;
            Q0=makeQuery(id+"F17.opExtrude","CAP_FACE",FACE,{"disambiguationData":[OSD([sQuery(id+"F16.wireOp",EDGE,"E144"),sQuery(id+"F16.wireOp",EDGE,"E145"),sQuery(id+"F16.wireOp",EDGE,"E146"),sQuery(id+"F16.wireOp",EDGE,"E147"),sQuery(id+"F16.wireOp",EDGE,"E148"),sQuery(id+"F16.wireOp",EDGE,"E149"),sQuery(id+"F16.wireOp",EDGE,"E150"),sQuery(id+"F16.wireOp",EDGE,"E151.MirrorCS"),sQuery(id+"F16.wireOp",EDGE,"E152.MirrorCS"),sQuery(id+"F16.wireOp",EDGE,"E153.MirrorCS"),sQuery(id+"F16.wireOp",EDGE,"E154.MirrorCS"),sQuery(id+"F16.wireOp",EDGE,"E155.MirrorCS"),sQuery(id+"F16.wireOp",EDGE,"E156.MirrorCS"),sQuery(id+"F16.wireOp",EDGE,"E157.MirrorCS")])],"isStart":false});
            var sketch = newSketch(context, id + "F19", { "sketchPlane" : qUnion([Q0])});
            skLineSegment(sketch, "E158", {"start": v(11, 14.3) * mm, "end": v(11, 55.97) * mm});
            skLineSegment(sketch, "E159", {"start": v(11, 55.97) * mm, "end": v(11.25, 55.88) * mm});
            skLineSegment(sketch, "E160", {"start": v(11.25, 55.88) * mm, "end": v(11.25, 14.3) * mm});
            skLineSegment(sketch, "E161", {"start": v(11.25, 14.3) * mm, "end": v(29.84, -18.48) * mm});
            skLineSegment(sketch, "E162", {"start": v(29.84, -18.48) * mm, "end": v(29.61, -18.58) * mm});
            skLineSegment(sketch, "E163", {"start": v(29.61, -18.58) * mm, "end": v(11.12, 14) * mm});
            skLineSegment(sketch, "E164.MirrorCS", {"start": v(-29.84, -18.48) * mm, "end": v(-29.61, -18.58) * mm});
            skLineSegment(sketch, "E165.MirrorCS", {"start": v(-11, 55.97) * mm, "end": v(-11.25, 55.88) * mm});
            skLineSegment(sketch, "E166.MirrorCS", {"start": v(-11, 14.3) * mm, "end": v(-11, 55.97) * mm});
            skLineSegment(sketch, "E167.MirrorCS", {"start": v(-11.25, 55.88) * mm, "end": v(-11.25, 14.3) * mm});
            skLineSegment(sketch, "E168.MirrorCS", {"start": v(-29.61, -18.58) * mm, "end": v(-11.12, 14) * mm});
            skLineSegment(sketch, "E169.MirrorCS", {"start": v(-11.25, 14.3) * mm, "end": v(-29.84, -18.48) * mm});
            skLineSegment(sketch, "E170", {"start": v(47.2, -10.57) * mm, "end": v(30, 19.75) * mm});
            skLineSegment(sketch, "E171", {"start": v(30, 19.75) * mm, "end": v(30, 53.14) * mm});
            skLineSegment(sketch, "E172", {"start": v(30, 53.14) * mm, "end": v(30.25, 53.1) * mm});
            skLineSegment(sketch, "E173", {"start": v(30.25, 53.1) * mm, "end": v(30.25, 19.81) * mm});
            skLineSegment(sketch, "E174", {"start": v(30.25, 19.81) * mm, "end": v(47.43, -10.47) * mm});
            skLineSegment(sketch, "E175", {"start": v(47.43, -10.47) * mm, "end": v(47.2, -10.57) * mm});
            skLineSegment(sketch, "E176.MirrorCS", {"start": v(-47.43, -10.47) * mm, "end": v(-47.2, -10.57) * mm});
            skLineSegment(sketch, "E177.MirrorCS", {"start": v(-30, 53.14) * mm, "end": v(-30.25, 53.1) * mm});
            skLineSegment(sketch, "E178.MirrorCS", {"start": v(-30, 19.75) * mm, "end": v(-30, 53.14) * mm});
            skLineSegment(sketch, "E179.MirrorCS", {"start": v(-30.25, 53.1) * mm, "end": v(-30.25, 19.81) * mm});
            skLineSegment(sketch, "E180.MirrorCS", {"start": v(-47.2, -10.57) * mm, "end": v(-30, 19.75) * mm});
            skLineSegment(sketch, "E181.MirrorCS", {"start": v(-30.25, 19.81) * mm, "end": v(-47.43, -10.47) * mm});
            skLineSegment(sketch, "E182", {"start": v(11.12, 14) * mm, "end": v(0, -5.46) * mm});
            skLineSegment(sketch, "E183", {"start": v(11, 14.3) * mm, "end": v(0, -4.96) * mm});
            skLineSegment(sketch, "E184.MirrorCS", {"start": v(-11.12, 14) * mm, "end": v(0, -5.46) * mm});
            skLineSegment(sketch, "E185.MirrorCS", {"start": v(-11, 14.3) * mm, "end": v(0, -4.96) * mm});
            skSolve(sketch);
        }
        {
            var Q0;
            Q0=qSketchRegion(id+"F19",true);
            extrude(context, id + "F20", {"entities" : qUnion([Q0]), "operationType" : NewBodyOperationType.REMOVE, "oppositeDirection" : true, "depth" : .5 * mm, "offsetDistance" : 25 * mm});
        }
        {
            var Q0;
            {var subQ0=sQuery(id+"F16.wireOp",EDGE,"E153.MirrorCS");var subQ1=sQuery(id+"F16.wireOp",EDGE,"E152.MirrorCS");var subQ2=sQuery(id+"F16.wireOp",EDGE,"E156.MirrorCS");var subQ3=sQuery(id+"F16.wireOp",EDGE,"E151.MirrorCS");var subQ4=sQuery(id+"F16.wireOp",EDGE,"E157.MirrorCS");Q0=makeQuery(id+"F20.boolean.opBoolean","SPLIT",FACE,{"disambiguationData":[TD([makeQuery(id+"F18.opFillet","BLEND_FACE",FACE,{"disambiguationData":[OSD([subQ0])]})])],"derivedFrom":makeQuery(id+"F17.opExtrude","CAP_FACE",FACE,{"disambiguationData":[OSD([sQuery(id+"F16.wireOp",EDGE,"E144"),sQuery(id+"F16.wireOp",EDGE,"E145"),sQuery(id+"F16.wireOp",EDGE,"E146"),sQuery(id+"F16.wireOp",EDGE,"E147"),sQuery(id+"F16.wireOp",EDGE,"E148"),sQuery(id+"F16.wireOp",EDGE,"E149"),sQuery(id+"F16.wireOp",EDGE,"E150"),subQ3,subQ1,subQ0,sQuery(id+"F16.wireOp",EDGE,"E154.MirrorCS"),sQuery(id+"F16.wireOp",EDGE,"E155.MirrorCS"),subQ2,subQ4])],"isStart":false})});}
            var Q1;
            {var subQ0=sQuery(id+"F16.wireOp",EDGE,"E152.MirrorCS");var subQ1=sQuery(id+"F16.wireOp",EDGE,"E151.MirrorCS");Q1=makeQuery(id+"F20.boolean.opBoolean","SPLIT",FACE,{"disambiguationData":[TD([makeQuery(id+"F20.opExtrude","SWEPT_FACE",FACE,{"disambiguationData":[OSD([sQuery(id+"F19.wireOp",EDGE,"E167.MirrorCS")])]})])],"derivedFrom":makeQuery(id+"F17.opExtrude","CAP_FACE",FACE,{"disambiguationData":[OSD([sQuery(id+"F16.wireOp",EDGE,"E144"),sQuery(id+"F16.wireOp",EDGE,"E145"),sQuery(id+"F16.wireOp",EDGE,"E146"),sQuery(id+"F16.wireOp",EDGE,"E147"),sQuery(id+"F16.wireOp",EDGE,"E148"),sQuery(id+"F16.wireOp",EDGE,"E149"),sQuery(id+"F16.wireOp",EDGE,"E150"),subQ1,subQ0,sQuery(id+"F16.wireOp",EDGE,"E153.MirrorCS"),sQuery(id+"F16.wireOp",EDGE,"E154.MirrorCS"),sQuery(id+"F16.wireOp",EDGE,"E155.MirrorCS"),sQuery(id+"F16.wireOp",EDGE,"E156.MirrorCS"),sQuery(id+"F16.wireOp",EDGE,"E157.MirrorCS")])],"isStart":false})});}
            var Q2;
            {var subQ0=sQuery(id+"F16.wireOp",EDGE,"E152.MirrorCS");var subQ1=sQuery(id+"F16.wireOp",EDGE,"E150");var subQ2=sQuery(id+"F16.wireOp",EDGE,"E154.MirrorCS");var subQ3=sQuery(id+"F16.wireOp",EDGE,"E149");Q2=makeQuery(id+"F20.boolean.opBoolean","SPLIT",FACE,{"disambiguationData":[TD([makeQuery(id+"F18.opFillet","BLEND_FACE",FACE,{"disambiguationData":[OSD([subQ1])]})])],"derivedFrom":makeQuery(id+"F17.opExtrude","CAP_FACE",FACE,{"disambiguationData":[OSD([sQuery(id+"F16.wireOp",EDGE,"E144"),sQuery(id+"F16.wireOp",EDGE,"E145"),sQuery(id+"F16.wireOp",EDGE,"E146"),sQuery(id+"F16.wireOp",EDGE,"E147"),sQuery(id+"F16.wireOp",EDGE,"E148"),subQ3,subQ1,sQuery(id+"F16.wireOp",EDGE,"E151.MirrorCS"),subQ0,sQuery(id+"F16.wireOp",EDGE,"E153.MirrorCS"),subQ2,sQuery(id+"F16.wireOp",EDGE,"E155.MirrorCS"),sQuery(id+"F16.wireOp",EDGE,"E156.MirrorCS"),sQuery(id+"F16.wireOp",EDGE,"E157.MirrorCS")])],"isStart":false})});}
            var Q3;
            {var subQ0=sQuery(id+"F16.wireOp",EDGE,"E151.MirrorCS");var subQ1=sQuery(id+"F16.wireOp",EDGE,"E155.MirrorCS");var subQ2=sQuery(id+"F16.wireOp",EDGE,"E144");var subQ3=sQuery(id+"F16.wireOp",EDGE,"E145");Q3=makeQuery(id+"F20.boolean.opBoolean","SPLIT",FACE,{"disambiguationData":[TD([makeQuery(id+"F18.opFillet","BLEND_FACE",FACE,{"disambiguationData":[OSD([subQ2])]})])],"derivedFrom":makeQuery(id+"F17.opExtrude","CAP_FACE",FACE,{"disambiguationData":[OSD([subQ2,subQ3,sQuery(id+"F16.wireOp",EDGE,"E146"),sQuery(id+"F16.wireOp",EDGE,"E147"),sQuery(id+"F16.wireOp",EDGE,"E148"),sQuery(id+"F16.wireOp",EDGE,"E149"),sQuery(id+"F16.wireOp",EDGE,"E150"),subQ0,sQuery(id+"F16.wireOp",EDGE,"E152.MirrorCS"),sQuery(id+"F16.wireOp",EDGE,"E153.MirrorCS"),sQuery(id+"F16.wireOp",EDGE,"E154.MirrorCS"),subQ1,sQuery(id+"F16.wireOp",EDGE,"E156.MirrorCS"),sQuery(id+"F16.wireOp",EDGE,"E157.MirrorCS")])],"isStart":false})});}
            var Q4;
            {var subQ0=sQuery(id+"F16.wireOp",EDGE,"E149");var subQ1=sQuery(id+"F16.wireOp",EDGE,"E145");Q4=makeQuery(id+"F20.boolean.opBoolean","SPLIT",FACE,{"disambiguationData":[TD([makeQuery(id+"F20.opExtrude","SWEPT_FACE",FACE,{"disambiguationData":[OSD([sQuery(id+"F19.wireOp",EDGE,"E160")])]})])],"derivedFrom":makeQuery(id+"F17.opExtrude","CAP_FACE",FACE,{"disambiguationData":[OSD([sQuery(id+"F16.wireOp",EDGE,"E144"),subQ1,sQuery(id+"F16.wireOp",EDGE,"E146"),sQuery(id+"F16.wireOp",EDGE,"E147"),sQuery(id+"F16.wireOp",EDGE,"E148"),subQ0,sQuery(id+"F16.wireOp",EDGE,"E150"),sQuery(id+"F16.wireOp",EDGE,"E151.MirrorCS"),sQuery(id+"F16.wireOp",EDGE,"E152.MirrorCS"),sQuery(id+"F16.wireOp",EDGE,"E153.MirrorCS"),sQuery(id+"F16.wireOp",EDGE,"E154.MirrorCS"),sQuery(id+"F16.wireOp",EDGE,"E155.MirrorCS"),sQuery(id+"F16.wireOp",EDGE,"E156.MirrorCS"),sQuery(id+"F16.wireOp",EDGE,"E157.MirrorCS")])],"isStart":false})});}
            var Q5;
            {var subQ0=sQuery(id+"F16.wireOp",EDGE,"E148");var subQ1=sQuery(id+"F16.wireOp",EDGE,"E147");var subQ2=sQuery(id+"F16.wireOp",EDGE,"E146");var subQ3=sQuery(id+"F16.wireOp",EDGE,"E145");var subQ4=sQuery(id+"F16.wireOp",EDGE,"E149");Q5=makeQuery(id+"F20.boolean.opBoolean","SPLIT",FACE,{"disambiguationData":[TD([makeQuery(id+"F18.opFillet","BLEND_FACE",FACE,{"disambiguationData":[OSD([subQ2])]})])],"derivedFrom":makeQuery(id+"F17.opExtrude","CAP_FACE",FACE,{"disambiguationData":[OSD([sQuery(id+"F16.wireOp",EDGE,"E144"),subQ3,subQ2,subQ1,subQ0,subQ4,sQuery(id+"F16.wireOp",EDGE,"E150"),sQuery(id+"F16.wireOp",EDGE,"E151.MirrorCS"),sQuery(id+"F16.wireOp",EDGE,"E152.MirrorCS"),sQuery(id+"F16.wireOp",EDGE,"E153.MirrorCS"),sQuery(id+"F16.wireOp",EDGE,"E154.MirrorCS"),sQuery(id+"F16.wireOp",EDGE,"E155.MirrorCS"),sQuery(id+"F16.wireOp",EDGE,"E156.MirrorCS"),sQuery(id+"F16.wireOp",EDGE,"E157.MirrorCS")])],"isStart":false})});}
            chamfer(context, id + "F21", {"entities" : qUnion([Q0, Q1, Q2, Q3, Q4, Q5]), "width" : .4 * mm, "tangentPropagation" : true});
        }
        {
            var Q0;
            Q0=makeQuery(id+"F17.opExtrude","CAP_FACE",FACE,{"disambiguationData":[OSD([sQuery(id+"F16.wireOp",EDGE,"E144"),sQuery(id+"F16.wireOp",EDGE,"E145"),sQuery(id+"F16.wireOp",EDGE,"E146"),sQuery(id+"F16.wireOp",EDGE,"E147"),sQuery(id+"F16.wireOp",EDGE,"E148"),sQuery(id+"F16.wireOp",EDGE,"E149"),sQuery(id+"F16.wireOp",EDGE,"E150"),sQuery(id+"F16.wireOp",EDGE,"E151.MirrorCS"),sQuery(id+"F16.wireOp",EDGE,"E152.MirrorCS"),sQuery(id+"F16.wireOp",EDGE,"E153.MirrorCS"),sQuery(id+"F16.wireOp",EDGE,"E154.MirrorCS"),sQuery(id+"F16.wireOp",EDGE,"E155.MirrorCS"),sQuery(id+"F16.wireOp",EDGE,"E156.MirrorCS"),sQuery(id+"F16.wireOp",EDGE,"E157.MirrorCS")])],"isStart":false});
            var sketch = newSketch(context, id + "F22", { "sketchPlane" : qUnion([Q0])});
            skLineSegment(sketch, "E186.bottom", {"start": v(43.63, 49.86) * mm, "end": v(46.48, 49.86) * mm});
            skLineSegment(sketch, "E186.top", {"start": v(43.63, 39.86) * mm, "end": v(46.48, 39.86) * mm});
            skLineSegment(sketch, "E186.left", {"start": v(43.63, 49.86) * mm, "end": v(43.63, 39.86) * mm});
            skLineSegment(sketch, "E186.right", {"start": v(46.48, 49.86) * mm, "end": v(46.48, 39.86) * mm});
            skLineSegment(sketch, "E187.bottom", {"start": v(53.95, 5.23) * mm, "end": v(56.95, 5.23) * mm});
            skLineSegment(sketch, "E187.top", {"start": v(53.95, -4.77) * mm, "end": v(56.95, -4.77) * mm});
            skLineSegment(sketch, "E187.left", {"start": v(53.95, 5.23) * mm, "end": v(53.95, -4.77) * mm});
            skLineSegment(sketch, "E187.right", {"start": v(56.95, 5.23) * mm, "end": v(56.95, -4.77) * mm});
            skLineSegment(sketch, "E188.MirrorCS", {"start": v(-53.95, -4.77) * mm, "end": v(-56.95, -4.77) * mm});
            skLineSegment(sketch, "E189.MirrorCS", {"start": v(-43.63, 39.86) * mm, "end": v(-46.48, 39.86) * mm});
            skLineSegment(sketch, "E190.MirrorCS", {"start": v(-43.63, 49.86) * mm, "end": v(-46.48, 49.86) * mm});
            skLineSegment(sketch, "E191.MirrorCS", {"start": v(-53.95, 5.23) * mm, "end": v(-56.95, 5.23) * mm});
            skLineSegment(sketch, "E192.MirrorCS", {"start": v(-56.95, 5.23) * mm, "end": v(-56.95, -4.77) * mm});
            skLineSegment(sketch, "E193.MirrorCS", {"start": v(-53.95, 5.23) * mm, "end": v(-53.95, -4.77) * mm});
            skLineSegment(sketch, "E194.MirrorCS", {"start": v(-43.63, 49.86) * mm, "end": v(-43.63, 39.86) * mm});
            skLineSegment(sketch, "E195.MirrorCS", {"start": v(-46.48, 49.86) * mm, "end": v(-46.48, 39.86) * mm});
            skSolve(sketch);
        }
        {
            var Q0;
            Q0=qSketchRegion(id+"F22",true);
            extrude(context, id + "F23", {"entities" : qUnion([Q0]), "operationType" : NewBodyOperationType.REMOVE, "oppositeDirection" : true, "depth" : 25 * mm, "offsetDistance" : 25 * mm, "symmetric" : true});
        }
        {
            var Q0;
            Q0=makeQuery(id+"F5.boolean.opBoolean","MERGE",FACE,{"derivedFrom":[makeQuery(id+"F3.opExtrude","CAP_FACE",FACE,{"disambiguationData":[OSD([sQuery(id+"F2.wireOp",EDGE,"E26"),sQuery(id+"F2.wireOp",EDGE,"E27"),sQuery(id+"F2.wireOp",EDGE,"E28"),sQuery(id+"F2.wireOp",EDGE,"E29"),sQuery(id+"F2.wireOp",EDGE,"E30"),sQuery(id+"F2.wireOp",EDGE,"E31"),sQuery(id+"F2.wireOp",EDGE,"E32"),sQuery(id+"F2.wireOp",EDGE,"E33"),sQuery(id+"F2.wireOp",EDGE,"E34"),sQuery(id+"F2.wireOp",EDGE,"E35"),sQuery(id+"F2.wireOp",EDGE,"E36"),sQuery(id+"F2.wireOp",EDGE,"E37"),sQuery(id+"F2.wireOp",EDGE,"E38"),sQuery(id+"F2.wireOp",EDGE,"E39"),sQuery(id+"F2.wireOp",EDGE,"E40.MirrorCS"),sQuery(id+"F2.wireOp",EDGE,"E41.MirrorCS"),sQuery(id+"F2.wireOp",EDGE,"E42.MirrorCS"),sQuery(id+"F2.wireOp",EDGE,"E43.MirrorCS"),sQuery(id+"F2.wireOp",EDGE,"E44.MirrorCS"),sQuery(id+"F2.wireOp",EDGE,"E45.MirrorCS"),sQuery(id+"F2.wireOp",EDGE,"E46.MirrorCS"),sQuery(id+"F2.wireOp",EDGE,"E47.MirrorCS"),sQuery(id+"F2.wireOp",EDGE,"E48.MirrorCS"),sQuery(id+"F2.wireOp",EDGE,"E49.MirrorCS"),sQuery(id+"F2.wireOp",EDGE,"E50.MirrorCS"),sQuery(id+"F2.wireOp",EDGE,"E51.MirrorCS"),sQuery(id+"F2.wireOp",EDGE,"E52.MirrorCS"),sQuery(id+"F2.wireOp",EDGE,"E53.MirrorCS")])],"isStart":false}),makeQuery(id+"F5.opExtrude","CAP_FACE",FACE,{"disambiguationData":[OSD([sQuery(id+"F4.wireOp",EDGE,"E54"),sQuery(id+"F4.wireOp",EDGE,"E55"),sQuery(id+"F4.wireOp",EDGE,"E56"),sQuery(id+"F4.wireOp",EDGE,"E57"),sQuery(id+"F4.wireOp",EDGE,"E58"),sQuery(id+"F4.wireOp",EDGE,"E59.MirrorCS"),sQuery(id+"F4.wireOp",EDGE,"E60.MirrorCS"),sQuery(id+"F4.wireOp",EDGE,"E61.MirrorCS"),sQuery(id+"F4.wireOp",EDGE,"E62.MirrorCS"),sQuery(id+"F4.wireOp",EDGE,"E63.MirrorCS")])],"isStart":false})]});
            var Q1;
            Q1=makeQuery(id+"F9.opExtrude","CAP_FACE",FACE,{"disambiguationData":[OSD([sQuery(id+"F8.wireOp",EDGE,"E82"),sQuery(id+"F8.wireOp",EDGE,"E83"),sQuery(id+"F8.wireOp",EDGE,"E84"),sQuery(id+"F8.wireOp",EDGE,"E85")])],"isStart":false});
            var Q2;
            Q2=makeQuery(id+"F7.opExtrude","CAP_FACE",FACE,{"disambiguationData":[OSD([sQuery(id+"F6.wireOp",EDGE,"E67"),sQuery(id+"F6.wireOp",EDGE,"E68"),sQuery(id+"F6.wireOp",EDGE,"E69"),sQuery(id+"F6.wireOp",EDGE,"E70"),sQuery(id+"F6.wireOp",EDGE,"E71"),sQuery(id+"F6.wireOp",EDGE,"E72")])],"isStart":false});
            var Q3;
            Q3=makeQuery(id+"F11.opExtrude","CAP_FACE",FACE,{"disambiguationData":[OSD([sQuery(id+"F10.wireOp",EDGE,"E90"),sQuery(id+"F10.wireOp",EDGE,"E91"),sQuery(id+"F10.wireOp",EDGE,"E92"),sQuery(id+"F10.wireOp",EDGE,"E93"),sQuery(id+"F10.wireOp",EDGE,"E94"),sQuery(id+"F10.wireOp",EDGE,"E95.MirrorCS"),sQuery(id+"F10.wireOp",EDGE,"E96.MirrorCS"),sQuery(id+"F10.wireOp",EDGE,"E97.MirrorCS"),sQuery(id+"F10.wireOp",EDGE,"E98.MirrorCS"),sQuery(id+"F10.wireOp",EDGE,"E99.MirrorCS")])],"isStart":false});
            var Q4;
            Q4=makeQuery(id+"F7.opExtrude","CAP_FACE",FACE,{"disambiguationData":[OSD([sQuery(id+"F6.wireOp",EDGE,"E64"),sQuery(id+"F6.wireOp",EDGE,"E65"),sQuery(id+"F6.wireOp",EDGE,"E66"),sQuery(id+"F6.wireOp",EDGE,"E75.MirrorCS"),sQuery(id+"F6.wireOp",EDGE,"E80.MirrorCS"),sQuery(id+"F6.wireOp",EDGE,"E81.MirrorCS")])],"isStart":false});
            var Q5;
            Q5=makeQuery(id+"F13.opExtrude","CAP_FACE",FACE,{"disambiguationData":[OSD([sQuery(id+"F12.wireOp",EDGE,"Hng6DFvr-lVOM-Odcz-qRKY-Kw1w4EjYl9qT"),sQuery(id+"F12.wireOp",EDGE,"M4bVsMzA-m1AL-o5a6-cRgY-HXBhoqxe6PO2"),sQuery(id+"F12.wireOp",EDGE,"16c2fec2-f32e-4c8d-a0f3-baa1978b9fef0.MirrorCS"),sQuery(id+"F12.wireOp",EDGE,"16c2fec2-f32e-4c8d-a0f3-baa1978b9fef1.MirrorCS")])],"isStart":false});
            var Q6;
            Q6=makeQuery(id+"F13.opExtrude","CAP_FACE",FACE,{"disambiguationData":[OSD([sQuery(id+"F12.wireOp",EDGE,"le7bHhup-nJOL-SFCl-Nu7f-rtTzvPoaqpXQ"),sQuery(id+"F12.wireOp",EDGE,"YBvBNWHm-rs8x-6Wrt-XOIs-9XtwNIGgoZkW"),sQuery(id+"F12.wireOp",EDGE,"mOkKRAbt-ATx1-DqhU-X6id-VtEa415OgW1E"),sQuery(id+"F12.wireOp",EDGE,"16c2fec2-f32e-4c8d-a0f3-baa1978b9fef2.MirrorCS"),sQuery(id+"F12.wireOp",EDGE,"16c2fec2-f32e-4c8d-a0f3-baa1978b9fef3.MirrorCS"),sQuery(id+"F12.wireOp",EDGE,"16c2fec2-f32e-4c8d-a0f3-baa1978b9fef4.MirrorCS")])],"isStart":false});
            var Q7;
            Q7=makeQuery(id+"F9.opExtrude","CAP_FACE",FACE,{"disambiguationData":[OSD([sQuery(id+"F8.wireOp",EDGE,"E86.MirrorCS"),sQuery(id+"F8.wireOp",EDGE,"E87.MirrorCS"),sQuery(id+"F8.wireOp",EDGE,"E88.MirrorCS"),sQuery(id+"F8.wireOp",EDGE,"E89.MirrorCS")])],"isStart":false});
            var Q8;
            Q8=makeQuery(id+"F7.opExtrude","CAP_FACE",FACE,{"disambiguationData":[OSD([sQuery(id+"F6.wireOp",EDGE,"E73.MirrorCS"),sQuery(id+"F6.wireOp",EDGE,"E74.MirrorCS"),sQuery(id+"F6.wireOp",EDGE,"E76.MirrorCS"),sQuery(id+"F6.wireOp",EDGE,"E77.MirrorCS"),sQuery(id+"F6.wireOp",EDGE,"E78.MirrorCS"),sQuery(id+"F6.wireOp",EDGE,"E79.MirrorCS")])],"isStart":false});
            chamfer(context, id + "F24", {"entities" : qUnion([Q0, Q1, Q2, Q3, Q4, Q5, Q6, Q7, Q8]), "width" : .5 * mm, "tangentPropagation" : true});
        }
        {
            var Q0;
            {var subQ0=sQuery(id+"F4.wireOp",EDGE,"E58");Q0=makeQuery(id+"F24.opChamfer","BLEND_EDGE",EDGE,{"blendedFrom":[makeQuery(id+"F5.opExtrude","CAP_EDGE",EDGE,{"disambiguationData":[OSD([subQ0])],"isStart":false}),makeQuery(id+"F5.boolean.opBoolean","MERGE",FACE,{"derivedFrom":[makeQuery(id+"F3.opExtrude","CAP_FACE",FACE,{"disambiguationData":[OSD([sQuery(id+"F2.wireOp",EDGE,"E26"),sQuery(id+"F2.wireOp",EDGE,"E27"),sQuery(id+"F2.wireOp",EDGE,"E28"),sQuery(id+"F2.wireOp",EDGE,"E29"),sQuery(id+"F2.wireOp",EDGE,"E30"),sQuery(id+"F2.wireOp",EDGE,"E31"),sQuery(id+"F2.wireOp",EDGE,"E32"),sQuery(id+"F2.wireOp",EDGE,"E33"),sQuery(id+"F2.wireOp",EDGE,"E34"),sQuery(id+"F2.wireOp",EDGE,"E35"),sQuery(id+"F2.wireOp",EDGE,"E36"),sQuery(id+"F2.wireOp",EDGE,"E37"),sQuery(id+"F2.wireOp",EDGE,"E38"),sQuery(id+"F2.wireOp",EDGE,"E39"),sQuery(id+"F2.wireOp",EDGE,"E40.MirrorCS"),sQuery(id+"F2.wireOp",EDGE,"E41.MirrorCS"),sQuery(id+"F2.wireOp",EDGE,"E42.MirrorCS"),sQuery(id+"F2.wireOp",EDGE,"E43.MirrorCS"),sQuery(id+"F2.wireOp",EDGE,"E44.MirrorCS"),sQuery(id+"F2.wireOp",EDGE,"E45.MirrorCS"),sQuery(id+"F2.wireOp",EDGE,"E46.MirrorCS"),sQuery(id+"F2.wireOp",EDGE,"E47.MirrorCS"),sQuery(id+"F2.wireOp",EDGE,"E48.MirrorCS"),sQuery(id+"F2.wireOp",EDGE,"E49.MirrorCS"),sQuery(id+"F2.wireOp",EDGE,"E50.MirrorCS"),sQuery(id+"F2.wireOp",EDGE,"E51.MirrorCS"),sQuery(id+"F2.wireOp",EDGE,"E52.MirrorCS"),sQuery(id+"F2.wireOp",EDGE,"E53.MirrorCS")])],"isStart":false}),makeQuery(id+"F5.opExtrude","CAP_FACE",FACE,{"disambiguationData":[OSD([sQuery(id+"F4.wireOp",EDGE,"E54"),sQuery(id+"F4.wireOp",EDGE,"E55"),sQuery(id+"F4.wireOp",EDGE,"E56"),sQuery(id+"F4.wireOp",EDGE,"E57"),subQ0,sQuery(id+"F4.wireOp",EDGE,"E59.MirrorCS"),sQuery(id+"F4.wireOp",EDGE,"E60.MirrorCS"),sQuery(id+"F4.wireOp",EDGE,"E61.MirrorCS"),sQuery(id+"F4.wireOp",EDGE,"E62.MirrorCS"),sQuery(id+"F4.wireOp",EDGE,"E63.MirrorCS")])],"isStart":false})]})],"blendedInto":[makeQuery(id+"F5.boolean.opBoolean","MERGE",FACE,{"derivedFrom":[makeQuery(id+"F3.opExtrude","CAP_FACE",FACE,{"disambiguationData":[OSD([sQuery(id+"F2.wireOp",EDGE,"E26"),sQuery(id+"F2.wireOp",EDGE,"E27"),sQuery(id+"F2.wireOp",EDGE,"E28"),sQuery(id+"F2.wireOp",EDGE,"E29"),sQuery(id+"F2.wireOp",EDGE,"E30"),sQuery(id+"F2.wireOp",EDGE,"E31"),sQuery(id+"F2.wireOp",EDGE,"E32"),sQuery(id+"F2.wireOp",EDGE,"E33"),sQuery(id+"F2.wireOp",EDGE,"E34"),sQuery(id+"F2.wireOp",EDGE,"E35"),sQuery(id+"F2.wireOp",EDGE,"E36"),sQuery(id+"F2.wireOp",EDGE,"E37"),sQuery(id+"F2.wireOp",EDGE,"E38"),sQuery(id+"F2.wireOp",EDGE,"E39"),sQuery(id+"F2.wireOp",EDGE,"E40.MirrorCS"),sQuery(id+"F2.wireOp",EDGE,"E41.MirrorCS"),sQuery(id+"F2.wireOp",EDGE,"E42.MirrorCS"),sQuery(id+"F2.wireOp",EDGE,"E43.MirrorCS"),sQuery(id+"F2.wireOp",EDGE,"E44.MirrorCS"),sQuery(id+"F2.wireOp",EDGE,"E45.MirrorCS"),sQuery(id+"F2.wireOp",EDGE,"E46.MirrorCS"),sQuery(id+"F2.wireOp",EDGE,"E47.MirrorCS"),sQuery(id+"F2.wireOp",EDGE,"E48.MirrorCS"),sQuery(id+"F2.wireOp",EDGE,"E49.MirrorCS"),sQuery(id+"F2.wireOp",EDGE,"E50.MirrorCS"),sQuery(id+"F2.wireOp",EDGE,"E51.MirrorCS"),sQuery(id+"F2.wireOp",EDGE,"E52.MirrorCS"),sQuery(id+"F2.wireOp",EDGE,"E53.MirrorCS")])],"isStart":false}),makeQuery(id+"F5.opExtrude","CAP_FACE",FACE,{"disambiguationData":[OSD([sQuery(id+"F4.wireOp",EDGE,"E54"),sQuery(id+"F4.wireOp",EDGE,"E55"),sQuery(id+"F4.wireOp",EDGE,"E56"),sQuery(id+"F4.wireOp",EDGE,"E57"),subQ0,sQuery(id+"F4.wireOp",EDGE,"E59.MirrorCS"),sQuery(id+"F4.wireOp",EDGE,"E60.MirrorCS"),sQuery(id+"F4.wireOp",EDGE,"E61.MirrorCS"),sQuery(id+"F4.wireOp",EDGE,"E62.MirrorCS"),sQuery(id+"F4.wireOp",EDGE,"E63.MirrorCS")])],"isStart":false})]})]});}
            var Q1;
            {var subQ0=sQuery(id+"F4.wireOp",EDGE,"E57");var subQ1=makeQuery(id+"F5.opExtrude","CAP_FACE",FACE,{"disambiguationData":[OSD([sQuery(id+"F4.wireOp",EDGE,"E54"),sQuery(id+"F4.wireOp",EDGE,"E55"),sQuery(id+"F4.wireOp",EDGE,"E56"),subQ0,sQuery(id+"F4.wireOp",EDGE,"E58"),sQuery(id+"F4.wireOp",EDGE,"E59.MirrorCS"),sQuery(id+"F4.wireOp",EDGE,"E60.MirrorCS"),sQuery(id+"F4.wireOp",EDGE,"E61.MirrorCS"),sQuery(id+"F4.wireOp",EDGE,"E62.MirrorCS"),sQuery(id+"F4.wireOp",EDGE,"E63.MirrorCS")])],"isStart":false});var subQ2=sQuery(id+"F2.wireOp",EDGE,"E27");var subQ3=sQuery(id+"F2.wireOp",EDGE,"E26");var subQ4=makeQuery(id+"F3.opExtrude","CAP_FACE",FACE,{"disambiguationData":[OSD([subQ3,subQ2,sQuery(id+"F2.wireOp",EDGE,"E28"),sQuery(id+"F2.wireOp",EDGE,"E29"),sQuery(id+"F2.wireOp",EDGE,"E30"),sQuery(id+"F2.wireOp",EDGE,"E31"),sQuery(id+"F2.wireOp",EDGE,"E32"),sQuery(id+"F2.wireOp",EDGE,"E33"),sQuery(id+"F2.wireOp",EDGE,"E34"),sQuery(id+"F2.wireOp",EDGE,"E35"),sQuery(id+"F2.wireOp",EDGE,"E36"),sQuery(id+"F2.wireOp",EDGE,"E37"),sQuery(id+"F2.wireOp",EDGE,"E38"),sQuery(id+"F2.wireOp",EDGE,"E39"),sQuery(id+"F2.wireOp",EDGE,"E40.MirrorCS"),sQuery(id+"F2.wireOp",EDGE,"E41.MirrorCS"),sQuery(id+"F2.wireOp",EDGE,"E42.MirrorCS"),sQuery(id+"F2.wireOp",EDGE,"E43.MirrorCS"),sQuery(id+"F2.wireOp",EDGE,"E44.MirrorCS"),sQuery(id+"F2.wireOp",EDGE,"E45.MirrorCS"),sQuery(id+"F2.wireOp",EDGE,"E46.MirrorCS"),sQuery(id+"F2.wireOp",EDGE,"E47.MirrorCS"),sQuery(id+"F2.wireOp",EDGE,"E48.MirrorCS"),sQuery(id+"F2.wireOp",EDGE,"E49.MirrorCS"),sQuery(id+"F2.wireOp",EDGE,"E50.MirrorCS"),sQuery(id+"F2.wireOp",EDGE,"E51.MirrorCS"),sQuery(id+"F2.wireOp",EDGE,"E52.MirrorCS"),sQuery(id+"F2.wireOp",EDGE,"E53.MirrorCS")])],"isStart":false});Q1=makeQuery(id+"F24.opChamfer","BLEND_EDGE",EDGE,{"blendedFrom":[makeQuery(id+"F5.boolean.opBoolean","SPLIT",EDGE,{"disambiguationData":[TD([makeQuery(id+"F3.opExtrude","SWEPT_FACE",FACE,{"disambiguationData":[OSD([subQ2])]})])],"derivedFrom":makeQuery(id+"F3.opExtrude","CAP_EDGE",EDGE,{"disambiguationData":[OSD([subQ3])],"isStart":false})}),makeQuery(id+"F5.boolean.opBoolean","MERGE",FACE,{"derivedFrom":[subQ4,subQ1]})],"blendedInto":[makeQuery(id+"F5.boolean.opBoolean","MERGE",FACE,{"derivedFrom":[subQ4,subQ1]})]});}
            var Q2;
            {var subQ0=sQuery(id+"F2.wireOp",EDGE,"E27");Q2=makeQuery(id+"F24.opChamfer","BLEND_EDGE",EDGE,{"blendedFrom":[makeQuery(id+"F3.opExtrude","CAP_EDGE",EDGE,{"disambiguationData":[OSD([subQ0])],"isStart":false}),makeQuery(id+"F5.boolean.opBoolean","MERGE",FACE,{"derivedFrom":[makeQuery(id+"F3.opExtrude","CAP_FACE",FACE,{"disambiguationData":[OSD([sQuery(id+"F2.wireOp",EDGE,"E26"),subQ0,sQuery(id+"F2.wireOp",EDGE,"E28"),sQuery(id+"F2.wireOp",EDGE,"E29"),sQuery(id+"F2.wireOp",EDGE,"E30"),sQuery(id+"F2.wireOp",EDGE,"E31"),sQuery(id+"F2.wireOp",EDGE,"E32"),sQuery(id+"F2.wireOp",EDGE,"E33"),sQuery(id+"F2.wireOp",EDGE,"E34"),sQuery(id+"F2.wireOp",EDGE,"E35"),sQuery(id+"F2.wireOp",EDGE,"E36"),sQuery(id+"F2.wireOp",EDGE,"E37"),sQuery(id+"F2.wireOp",EDGE,"E38"),sQuery(id+"F2.wireOp",EDGE,"E39"),sQuery(id+"F2.wireOp",EDGE,"E40.MirrorCS"),sQuery(id+"F2.wireOp",EDGE,"E41.MirrorCS"),sQuery(id+"F2.wireOp",EDGE,"E42.MirrorCS"),sQuery(id+"F2.wireOp",EDGE,"E43.MirrorCS"),sQuery(id+"F2.wireOp",EDGE,"E44.MirrorCS"),sQuery(id+"F2.wireOp",EDGE,"E45.MirrorCS"),sQuery(id+"F2.wireOp",EDGE,"E46.MirrorCS"),sQuery(id+"F2.wireOp",EDGE,"E47.MirrorCS"),sQuery(id+"F2.wireOp",EDGE,"E48.MirrorCS"),sQuery(id+"F2.wireOp",EDGE,"E49.MirrorCS"),sQuery(id+"F2.wireOp",EDGE,"E50.MirrorCS"),sQuery(id+"F2.wireOp",EDGE,"E51.MirrorCS"),sQuery(id+"F2.wireOp",EDGE,"E52.MirrorCS"),sQuery(id+"F2.wireOp",EDGE,"E53.MirrorCS")])],"isStart":false}),makeQuery(id+"F5.opExtrude","CAP_FACE",FACE,{"disambiguationData":[OSD([sQuery(id+"F4.wireOp",EDGE,"E54"),sQuery(id+"F4.wireOp",EDGE,"E55"),sQuery(id+"F4.wireOp",EDGE,"E56"),sQuery(id+"F4.wireOp",EDGE,"E57"),sQuery(id+"F4.wireOp",EDGE,"E58"),sQuery(id+"F4.wireOp",EDGE,"E59.MirrorCS"),sQuery(id+"F4.wireOp",EDGE,"E60.MirrorCS"),sQuery(id+"F4.wireOp",EDGE,"E61.MirrorCS"),sQuery(id+"F4.wireOp",EDGE,"E62.MirrorCS"),sQuery(id+"F4.wireOp",EDGE,"E63.MirrorCS")])],"isStart":false})]})],"blendedInto":[makeQuery(id+"F5.boolean.opBoolean","MERGE",FACE,{"derivedFrom":[makeQuery(id+"F3.opExtrude","CAP_FACE",FACE,{"disambiguationData":[OSD([sQuery(id+"F2.wireOp",EDGE,"E26"),subQ0,sQuery(id+"F2.wireOp",EDGE,"E28"),sQuery(id+"F2.wireOp",EDGE,"E29"),sQuery(id+"F2.wireOp",EDGE,"E30"),sQuery(id+"F2.wireOp",EDGE,"E31"),sQuery(id+"F2.wireOp",EDGE,"E32"),sQuery(id+"F2.wireOp",EDGE,"E33"),sQuery(id+"F2.wireOp",EDGE,"E34"),sQuery(id+"F2.wireOp",EDGE,"E35"),sQuery(id+"F2.wireOp",EDGE,"E36"),sQuery(id+"F2.wireOp",EDGE,"E37"),sQuery(id+"F2.wireOp",EDGE,"E38"),sQuery(id+"F2.wireOp",EDGE,"E39"),sQuery(id+"F2.wireOp",EDGE,"E40.MirrorCS"),sQuery(id+"F2.wireOp",EDGE,"E41.MirrorCS"),sQuery(id+"F2.wireOp",EDGE,"E42.MirrorCS"),sQuery(id+"F2.wireOp",EDGE,"E43.MirrorCS"),sQuery(id+"F2.wireOp",EDGE,"E44.MirrorCS"),sQuery(id+"F2.wireOp",EDGE,"E45.MirrorCS"),sQuery(id+"F2.wireOp",EDGE,"E46.MirrorCS"),sQuery(id+"F2.wireOp",EDGE,"E47.MirrorCS"),sQuery(id+"F2.wireOp",EDGE,"E48.MirrorCS"),sQuery(id+"F2.wireOp",EDGE,"E49.MirrorCS"),sQuery(id+"F2.wireOp",EDGE,"E50.MirrorCS"),sQuery(id+"F2.wireOp",EDGE,"E51.MirrorCS"),sQuery(id+"F2.wireOp",EDGE,"E52.MirrorCS"),sQuery(id+"F2.wireOp",EDGE,"E53.MirrorCS")])],"isStart":false}),makeQuery(id+"F5.opExtrude","CAP_FACE",FACE,{"disambiguationData":[OSD([sQuery(id+"F4.wireOp",EDGE,"E54"),sQuery(id+"F4.wireOp",EDGE,"E55"),sQuery(id+"F4.wireOp",EDGE,"E56"),sQuery(id+"F4.wireOp",EDGE,"E57"),sQuery(id+"F4.wireOp",EDGE,"E58"),sQuery(id+"F4.wireOp",EDGE,"E59.MirrorCS"),sQuery(id+"F4.wireOp",EDGE,"E60.MirrorCS"),sQuery(id+"F4.wireOp",EDGE,"E61.MirrorCS"),sQuery(id+"F4.wireOp",EDGE,"E62.MirrorCS"),sQuery(id+"F4.wireOp",EDGE,"E63.MirrorCS")])],"isStart":false})]})]});}
            var Q3;
            {var subQ0=sQuery(id+"F2.wireOp",EDGE,"E28");Q3=makeQuery(id+"F24.opChamfer","BLEND_EDGE",EDGE,{"blendedFrom":[makeQuery(id+"F3.opExtrude","CAP_EDGE",EDGE,{"disambiguationData":[OSD([subQ0])],"isStart":false}),makeQuery(id+"F5.boolean.opBoolean","MERGE",FACE,{"derivedFrom":[makeQuery(id+"F3.opExtrude","CAP_FACE",FACE,{"disambiguationData":[OSD([sQuery(id+"F2.wireOp",EDGE,"E26"),sQuery(id+"F2.wireOp",EDGE,"E27"),subQ0,sQuery(id+"F2.wireOp",EDGE,"E29"),sQuery(id+"F2.wireOp",EDGE,"E30"),sQuery(id+"F2.wireOp",EDGE,"E31"),sQuery(id+"F2.wireOp",EDGE,"E32"),sQuery(id+"F2.wireOp",EDGE,"E33"),sQuery(id+"F2.wireOp",EDGE,"E34"),sQuery(id+"F2.wireOp",EDGE,"E35"),sQuery(id+"F2.wireOp",EDGE,"E36"),sQuery(id+"F2.wireOp",EDGE,"E37"),sQuery(id+"F2.wireOp",EDGE,"E38"),sQuery(id+"F2.wireOp",EDGE,"E39"),sQuery(id+"F2.wireOp",EDGE,"E40.MirrorCS"),sQuery(id+"F2.wireOp",EDGE,"E41.MirrorCS"),sQuery(id+"F2.wireOp",EDGE,"E42.MirrorCS"),sQuery(id+"F2.wireOp",EDGE,"E43.MirrorCS"),sQuery(id+"F2.wireOp",EDGE,"E44.MirrorCS"),sQuery(id+"F2.wireOp",EDGE,"E45.MirrorCS"),sQuery(id+"F2.wireOp",EDGE,"E46.MirrorCS"),sQuery(id+"F2.wireOp",EDGE,"E47.MirrorCS"),sQuery(id+"F2.wireOp",EDGE,"E48.MirrorCS"),sQuery(id+"F2.wireOp",EDGE,"E49.MirrorCS"),sQuery(id+"F2.wireOp",EDGE,"E50.MirrorCS"),sQuery(id+"F2.wireOp",EDGE,"E51.MirrorCS"),sQuery(id+"F2.wireOp",EDGE,"E52.MirrorCS"),sQuery(id+"F2.wireOp",EDGE,"E53.MirrorCS")])],"isStart":false}),makeQuery(id+"F5.opExtrude","CAP_FACE",FACE,{"disambiguationData":[OSD([sQuery(id+"F4.wireOp",EDGE,"E54"),sQuery(id+"F4.wireOp",EDGE,"E55"),sQuery(id+"F4.wireOp",EDGE,"E56"),sQuery(id+"F4.wireOp",EDGE,"E57"),sQuery(id+"F4.wireOp",EDGE,"E58"),sQuery(id+"F4.wireOp",EDGE,"E59.MirrorCS"),sQuery(id+"F4.wireOp",EDGE,"E60.MirrorCS"),sQuery(id+"F4.wireOp",EDGE,"E61.MirrorCS"),sQuery(id+"F4.wireOp",EDGE,"E62.MirrorCS"),sQuery(id+"F4.wireOp",EDGE,"E63.MirrorCS")])],"isStart":false})]})],"blendedInto":[makeQuery(id+"F5.boolean.opBoolean","MERGE",FACE,{"derivedFrom":[makeQuery(id+"F3.opExtrude","CAP_FACE",FACE,{"disambiguationData":[OSD([sQuery(id+"F2.wireOp",EDGE,"E26"),sQuery(id+"F2.wireOp",EDGE,"E27"),subQ0,sQuery(id+"F2.wireOp",EDGE,"E29"),sQuery(id+"F2.wireOp",EDGE,"E30"),sQuery(id+"F2.wireOp",EDGE,"E31"),sQuery(id+"F2.wireOp",EDGE,"E32"),sQuery(id+"F2.wireOp",EDGE,"E33"),sQuery(id+"F2.wireOp",EDGE,"E34"),sQuery(id+"F2.wireOp",EDGE,"E35"),sQuery(id+"F2.wireOp",EDGE,"E36"),sQuery(id+"F2.wireOp",EDGE,"E37"),sQuery(id+"F2.wireOp",EDGE,"E38"),sQuery(id+"F2.wireOp",EDGE,"E39"),sQuery(id+"F2.wireOp",EDGE,"E40.MirrorCS"),sQuery(id+"F2.wireOp",EDGE,"E41.MirrorCS"),sQuery(id+"F2.wireOp",EDGE,"E42.MirrorCS"),sQuery(id+"F2.wireOp",EDGE,"E43.MirrorCS"),sQuery(id+"F2.wireOp",EDGE,"E44.MirrorCS"),sQuery(id+"F2.wireOp",EDGE,"E45.MirrorCS"),sQuery(id+"F2.wireOp",EDGE,"E46.MirrorCS"),sQuery(id+"F2.wireOp",EDGE,"E47.MirrorCS"),sQuery(id+"F2.wireOp",EDGE,"E48.MirrorCS"),sQuery(id+"F2.wireOp",EDGE,"E49.MirrorCS"),sQuery(id+"F2.wireOp",EDGE,"E50.MirrorCS"),sQuery(id+"F2.wireOp",EDGE,"E51.MirrorCS"),sQuery(id+"F2.wireOp",EDGE,"E52.MirrorCS"),sQuery(id+"F2.wireOp",EDGE,"E53.MirrorCS")])],"isStart":false}),makeQuery(id+"F5.opExtrude","CAP_FACE",FACE,{"disambiguationData":[OSD([sQuery(id+"F4.wireOp",EDGE,"E54"),sQuery(id+"F4.wireOp",EDGE,"E55"),sQuery(id+"F4.wireOp",EDGE,"E56"),sQuery(id+"F4.wireOp",EDGE,"E57"),sQuery(id+"F4.wireOp",EDGE,"E58"),sQuery(id+"F4.wireOp",EDGE,"E59.MirrorCS"),sQuery(id+"F4.wireOp",EDGE,"E60.MirrorCS"),sQuery(id+"F4.wireOp",EDGE,"E61.MirrorCS"),sQuery(id+"F4.wireOp",EDGE,"E62.MirrorCS"),sQuery(id+"F4.wireOp",EDGE,"E63.MirrorCS")])],"isStart":false})]})]});}
            var Q4;
            {var subQ0=sQuery(id+"F2.wireOp",EDGE,"E29");Q4=makeQuery(id+"F24.opChamfer","BLEND_EDGE",EDGE,{"blendedFrom":[makeQuery(id+"F3.opExtrude","CAP_EDGE",EDGE,{"disambiguationData":[OSD([subQ0])],"isStart":false}),makeQuery(id+"F5.boolean.opBoolean","MERGE",FACE,{"derivedFrom":[makeQuery(id+"F3.opExtrude","CAP_FACE",FACE,{"disambiguationData":[OSD([sQuery(id+"F2.wireOp",EDGE,"E26"),sQuery(id+"F2.wireOp",EDGE,"E27"),sQuery(id+"F2.wireOp",EDGE,"E28"),subQ0,sQuery(id+"F2.wireOp",EDGE,"E30"),sQuery(id+"F2.wireOp",EDGE,"E31"),sQuery(id+"F2.wireOp",EDGE,"E32"),sQuery(id+"F2.wireOp",EDGE,"E33"),sQuery(id+"F2.wireOp",EDGE,"E34"),sQuery(id+"F2.wireOp",EDGE,"E35"),sQuery(id+"F2.wireOp",EDGE,"E36"),sQuery(id+"F2.wireOp",EDGE,"E37"),sQuery(id+"F2.wireOp",EDGE,"E38"),sQuery(id+"F2.wireOp",EDGE,"E39"),sQuery(id+"F2.wireOp",EDGE,"E40.MirrorCS"),sQuery(id+"F2.wireOp",EDGE,"E41.MirrorCS"),sQuery(id+"F2.wireOp",EDGE,"E42.MirrorCS"),sQuery(id+"F2.wireOp",EDGE,"E43.MirrorCS"),sQuery(id+"F2.wireOp",EDGE,"E44.MirrorCS"),sQuery(id+"F2.wireOp",EDGE,"E45.MirrorCS"),sQuery(id+"F2.wireOp",EDGE,"E46.MirrorCS"),sQuery(id+"F2.wireOp",EDGE,"E47.MirrorCS"),sQuery(id+"F2.wireOp",EDGE,"E48.MirrorCS"),sQuery(id+"F2.wireOp",EDGE,"E49.MirrorCS"),sQuery(id+"F2.wireOp",EDGE,"E50.MirrorCS"),sQuery(id+"F2.wireOp",EDGE,"E51.MirrorCS"),sQuery(id+"F2.wireOp",EDGE,"E52.MirrorCS"),sQuery(id+"F2.wireOp",EDGE,"E53.MirrorCS")])],"isStart":false}),makeQuery(id+"F5.opExtrude","CAP_FACE",FACE,{"disambiguationData":[OSD([sQuery(id+"F4.wireOp",EDGE,"E54"),sQuery(id+"F4.wireOp",EDGE,"E55"),sQuery(id+"F4.wireOp",EDGE,"E56"),sQuery(id+"F4.wireOp",EDGE,"E57"),sQuery(id+"F4.wireOp",EDGE,"E58"),sQuery(id+"F4.wireOp",EDGE,"E59.MirrorCS"),sQuery(id+"F4.wireOp",EDGE,"E60.MirrorCS"),sQuery(id+"F4.wireOp",EDGE,"E61.MirrorCS"),sQuery(id+"F4.wireOp",EDGE,"E62.MirrorCS"),sQuery(id+"F4.wireOp",EDGE,"E63.MirrorCS")])],"isStart":false})]})],"blendedInto":[makeQuery(id+"F5.boolean.opBoolean","MERGE",FACE,{"derivedFrom":[makeQuery(id+"F3.opExtrude","CAP_FACE",FACE,{"disambiguationData":[OSD([sQuery(id+"F2.wireOp",EDGE,"E26"),sQuery(id+"F2.wireOp",EDGE,"E27"),sQuery(id+"F2.wireOp",EDGE,"E28"),subQ0,sQuery(id+"F2.wireOp",EDGE,"E30"),sQuery(id+"F2.wireOp",EDGE,"E31"),sQuery(id+"F2.wireOp",EDGE,"E32"),sQuery(id+"F2.wireOp",EDGE,"E33"),sQuery(id+"F2.wireOp",EDGE,"E34"),sQuery(id+"F2.wireOp",EDGE,"E35"),sQuery(id+"F2.wireOp",EDGE,"E36"),sQuery(id+"F2.wireOp",EDGE,"E37"),sQuery(id+"F2.wireOp",EDGE,"E38"),sQuery(id+"F2.wireOp",EDGE,"E39"),sQuery(id+"F2.wireOp",EDGE,"E40.MirrorCS"),sQuery(id+"F2.wireOp",EDGE,"E41.MirrorCS"),sQuery(id+"F2.wireOp",EDGE,"E42.MirrorCS"),sQuery(id+"F2.wireOp",EDGE,"E43.MirrorCS"),sQuery(id+"F2.wireOp",EDGE,"E44.MirrorCS"),sQuery(id+"F2.wireOp",EDGE,"E45.MirrorCS"),sQuery(id+"F2.wireOp",EDGE,"E46.MirrorCS"),sQuery(id+"F2.wireOp",EDGE,"E47.MirrorCS"),sQuery(id+"F2.wireOp",EDGE,"E48.MirrorCS"),sQuery(id+"F2.wireOp",EDGE,"E49.MirrorCS"),sQuery(id+"F2.wireOp",EDGE,"E50.MirrorCS"),sQuery(id+"F2.wireOp",EDGE,"E51.MirrorCS"),sQuery(id+"F2.wireOp",EDGE,"E52.MirrorCS"),sQuery(id+"F2.wireOp",EDGE,"E53.MirrorCS")])],"isStart":false}),makeQuery(id+"F5.opExtrude","CAP_FACE",FACE,{"disambiguationData":[OSD([sQuery(id+"F4.wireOp",EDGE,"E54"),sQuery(id+"F4.wireOp",EDGE,"E55"),sQuery(id+"F4.wireOp",EDGE,"E56"),sQuery(id+"F4.wireOp",EDGE,"E57"),sQuery(id+"F4.wireOp",EDGE,"E58"),sQuery(id+"F4.wireOp",EDGE,"E59.MirrorCS"),sQuery(id+"F4.wireOp",EDGE,"E60.MirrorCS"),sQuery(id+"F4.wireOp",EDGE,"E61.MirrorCS"),sQuery(id+"F4.wireOp",EDGE,"E62.MirrorCS"),sQuery(id+"F4.wireOp",EDGE,"E63.MirrorCS")])],"isStart":false})]})]});}
            var Q5;
            {var subQ0=sQuery(id+"F6.wireOp",EDGE,"E64");Q5=makeQuery(id+"F24.opChamfer","BLEND_EDGE",EDGE,{"blendedFrom":[makeQuery(id+"F7.opExtrude","CAP_EDGE",EDGE,{"disambiguationData":[OSD([subQ0])],"isStart":false}),makeQuery(id+"F7.opExtrude","CAP_FACE",FACE,{"disambiguationData":[OSD([subQ0,sQuery(id+"F6.wireOp",EDGE,"E65"),sQuery(id+"F6.wireOp",EDGE,"E66"),sQuery(id+"F6.wireOp",EDGE,"E75.MirrorCS"),sQuery(id+"F6.wireOp",EDGE,"E80.MirrorCS"),sQuery(id+"F6.wireOp",EDGE,"E81.MirrorCS")])],"isStart":false})],"blendedInto":[makeQuery(id+"F7.opExtrude","CAP_FACE",FACE,{"disambiguationData":[OSD([subQ0,sQuery(id+"F6.wireOp",EDGE,"E65"),sQuery(id+"F6.wireOp",EDGE,"E66"),sQuery(id+"F6.wireOp",EDGE,"E75.MirrorCS"),sQuery(id+"F6.wireOp",EDGE,"E80.MirrorCS"),sQuery(id+"F6.wireOp",EDGE,"E81.MirrorCS")])],"isStart":false})]});}
            var Q6;
            {var subQ0=sQuery(id+"F6.wireOp",EDGE,"E81.MirrorCS");Q6=makeQuery(id+"F24.opChamfer","BLEND_EDGE",EDGE,{"blendedFrom":[makeQuery(id+"F7.opExtrude","CAP_EDGE",EDGE,{"disambiguationData":[OSD([subQ0])],"isStart":false}),makeQuery(id+"F7.opExtrude","CAP_FACE",FACE,{"disambiguationData":[OSD([sQuery(id+"F6.wireOp",EDGE,"E64"),sQuery(id+"F6.wireOp",EDGE,"E65"),sQuery(id+"F6.wireOp",EDGE,"E66"),sQuery(id+"F6.wireOp",EDGE,"E75.MirrorCS"),sQuery(id+"F6.wireOp",EDGE,"E80.MirrorCS"),subQ0])],"isStart":false})],"blendedInto":[makeQuery(id+"F7.opExtrude","CAP_FACE",FACE,{"disambiguationData":[OSD([sQuery(id+"F6.wireOp",EDGE,"E64"),sQuery(id+"F6.wireOp",EDGE,"E65"),sQuery(id+"F6.wireOp",EDGE,"E66"),sQuery(id+"F6.wireOp",EDGE,"E75.MirrorCS"),sQuery(id+"F6.wireOp",EDGE,"E80.MirrorCS"),subQ0])],"isStart":false})]});}
            var Q7;
            {var subQ0=sQuery(id+"F2.wireOp",EDGE,"E43.MirrorCS");Q7=makeQuery(id+"F24.opChamfer","BLEND_EDGE",EDGE,{"blendedFrom":[makeQuery(id+"F3.opExtrude","CAP_EDGE",EDGE,{"disambiguationData":[OSD([subQ0])],"isStart":false}),makeQuery(id+"F5.boolean.opBoolean","MERGE",FACE,{"derivedFrom":[makeQuery(id+"F3.opExtrude","CAP_FACE",FACE,{"disambiguationData":[OSD([sQuery(id+"F2.wireOp",EDGE,"E26"),sQuery(id+"F2.wireOp",EDGE,"E27"),sQuery(id+"F2.wireOp",EDGE,"E28"),sQuery(id+"F2.wireOp",EDGE,"E29"),sQuery(id+"F2.wireOp",EDGE,"E30"),sQuery(id+"F2.wireOp",EDGE,"E31"),sQuery(id+"F2.wireOp",EDGE,"E32"),sQuery(id+"F2.wireOp",EDGE,"E33"),sQuery(id+"F2.wireOp",EDGE,"E34"),sQuery(id+"F2.wireOp",EDGE,"E35"),sQuery(id+"F2.wireOp",EDGE,"E36"),sQuery(id+"F2.wireOp",EDGE,"E37"),sQuery(id+"F2.wireOp",EDGE,"E38"),sQuery(id+"F2.wireOp",EDGE,"E39"),sQuery(id+"F2.wireOp",EDGE,"E40.MirrorCS"),sQuery(id+"F2.wireOp",EDGE,"E41.MirrorCS"),sQuery(id+"F2.wireOp",EDGE,"E42.MirrorCS"),subQ0,sQuery(id+"F2.wireOp",EDGE,"E44.MirrorCS"),sQuery(id+"F2.wireOp",EDGE,"E45.MirrorCS"),sQuery(id+"F2.wireOp",EDGE,"E46.MirrorCS"),sQuery(id+"F2.wireOp",EDGE,"E47.MirrorCS"),sQuery(id+"F2.wireOp",EDGE,"E48.MirrorCS"),sQuery(id+"F2.wireOp",EDGE,"E49.MirrorCS"),sQuery(id+"F2.wireOp",EDGE,"E50.MirrorCS"),sQuery(id+"F2.wireOp",EDGE,"E51.MirrorCS"),sQuery(id+"F2.wireOp",EDGE,"E52.MirrorCS"),sQuery(id+"F2.wireOp",EDGE,"E53.MirrorCS")])],"isStart":false}),makeQuery(id+"F5.opExtrude","CAP_FACE",FACE,{"disambiguationData":[OSD([sQuery(id+"F4.wireOp",EDGE,"E54"),sQuery(id+"F4.wireOp",EDGE,"E55"),sQuery(id+"F4.wireOp",EDGE,"E56"),sQuery(id+"F4.wireOp",EDGE,"E57"),sQuery(id+"F4.wireOp",EDGE,"E58"),sQuery(id+"F4.wireOp",EDGE,"E59.MirrorCS"),sQuery(id+"F4.wireOp",EDGE,"E60.MirrorCS"),sQuery(id+"F4.wireOp",EDGE,"E61.MirrorCS"),sQuery(id+"F4.wireOp",EDGE,"E62.MirrorCS"),sQuery(id+"F4.wireOp",EDGE,"E63.MirrorCS")])],"isStart":false})]})],"blendedInto":[makeQuery(id+"F5.boolean.opBoolean","MERGE",FACE,{"derivedFrom":[makeQuery(id+"F3.opExtrude","CAP_FACE",FACE,{"disambiguationData":[OSD([sQuery(id+"F2.wireOp",EDGE,"E26"),sQuery(id+"F2.wireOp",EDGE,"E27"),sQuery(id+"F2.wireOp",EDGE,"E28"),sQuery(id+"F2.wireOp",EDGE,"E29"),sQuery(id+"F2.wireOp",EDGE,"E30"),sQuery(id+"F2.wireOp",EDGE,"E31"),sQuery(id+"F2.wireOp",EDGE,"E32"),sQuery(id+"F2.wireOp",EDGE,"E33"),sQuery(id+"F2.wireOp",EDGE,"E34"),sQuery(id+"F2.wireOp",EDGE,"E35"),sQuery(id+"F2.wireOp",EDGE,"E36"),sQuery(id+"F2.wireOp",EDGE,"E37"),sQuery(id+"F2.wireOp",EDGE,"E38"),sQuery(id+"F2.wireOp",EDGE,"E39"),sQuery(id+"F2.wireOp",EDGE,"E40.MirrorCS"),sQuery(id+"F2.wireOp",EDGE,"E41.MirrorCS"),sQuery(id+"F2.wireOp",EDGE,"E42.MirrorCS"),subQ0,sQuery(id+"F2.wireOp",EDGE,"E44.MirrorCS"),sQuery(id+"F2.wireOp",EDGE,"E45.MirrorCS"),sQuery(id+"F2.wireOp",EDGE,"E46.MirrorCS"),sQuery(id+"F2.wireOp",EDGE,"E47.MirrorCS"),sQuery(id+"F2.wireOp",EDGE,"E48.MirrorCS"),sQuery(id+"F2.wireOp",EDGE,"E49.MirrorCS"),sQuery(id+"F2.wireOp",EDGE,"E50.MirrorCS"),sQuery(id+"F2.wireOp",EDGE,"E51.MirrorCS"),sQuery(id+"F2.wireOp",EDGE,"E52.MirrorCS"),sQuery(id+"F2.wireOp",EDGE,"E53.MirrorCS")])],"isStart":false}),makeQuery(id+"F5.opExtrude","CAP_FACE",FACE,{"disambiguationData":[OSD([sQuery(id+"F4.wireOp",EDGE,"E54"),sQuery(id+"F4.wireOp",EDGE,"E55"),sQuery(id+"F4.wireOp",EDGE,"E56"),sQuery(id+"F4.wireOp",EDGE,"E57"),sQuery(id+"F4.wireOp",EDGE,"E58"),sQuery(id+"F4.wireOp",EDGE,"E59.MirrorCS"),sQuery(id+"F4.wireOp",EDGE,"E60.MirrorCS"),sQuery(id+"F4.wireOp",EDGE,"E61.MirrorCS"),sQuery(id+"F4.wireOp",EDGE,"E62.MirrorCS"),sQuery(id+"F4.wireOp",EDGE,"E63.MirrorCS")])],"isStart":false})]})]});}
            var Q8;
            {var subQ0=sQuery(id+"F2.wireOp",EDGE,"E42.MirrorCS");Q8=makeQuery(id+"F24.opChamfer","BLEND_EDGE",EDGE,{"blendedFrom":[makeQuery(id+"F3.opExtrude","CAP_EDGE",EDGE,{"disambiguationData":[OSD([subQ0])],"isStart":false}),makeQuery(id+"F5.boolean.opBoolean","MERGE",FACE,{"derivedFrom":[makeQuery(id+"F3.opExtrude","CAP_FACE",FACE,{"disambiguationData":[OSD([sQuery(id+"F2.wireOp",EDGE,"E26"),sQuery(id+"F2.wireOp",EDGE,"E27"),sQuery(id+"F2.wireOp",EDGE,"E28"),sQuery(id+"F2.wireOp",EDGE,"E29"),sQuery(id+"F2.wireOp",EDGE,"E30"),sQuery(id+"F2.wireOp",EDGE,"E31"),sQuery(id+"F2.wireOp",EDGE,"E32"),sQuery(id+"F2.wireOp",EDGE,"E33"),sQuery(id+"F2.wireOp",EDGE,"E34"),sQuery(id+"F2.wireOp",EDGE,"E35"),sQuery(id+"F2.wireOp",EDGE,"E36"),sQuery(id+"F2.wireOp",EDGE,"E37"),sQuery(id+"F2.wireOp",EDGE,"E38"),sQuery(id+"F2.wireOp",EDGE,"E39"),sQuery(id+"F2.wireOp",EDGE,"E40.MirrorCS"),sQuery(id+"F2.wireOp",EDGE,"E41.MirrorCS"),subQ0,sQuery(id+"F2.wireOp",EDGE,"E43.MirrorCS"),sQuery(id+"F2.wireOp",EDGE,"E44.MirrorCS"),sQuery(id+"F2.wireOp",EDGE,"E45.MirrorCS"),sQuery(id+"F2.wireOp",EDGE,"E46.MirrorCS"),sQuery(id+"F2.wireOp",EDGE,"E47.MirrorCS"),sQuery(id+"F2.wireOp",EDGE,"E48.MirrorCS"),sQuery(id+"F2.wireOp",EDGE,"E49.MirrorCS"),sQuery(id+"F2.wireOp",EDGE,"E50.MirrorCS"),sQuery(id+"F2.wireOp",EDGE,"E51.MirrorCS"),sQuery(id+"F2.wireOp",EDGE,"E52.MirrorCS"),sQuery(id+"F2.wireOp",EDGE,"E53.MirrorCS")])],"isStart":false}),makeQuery(id+"F5.opExtrude","CAP_FACE",FACE,{"disambiguationData":[OSD([sQuery(id+"F4.wireOp",EDGE,"E54"),sQuery(id+"F4.wireOp",EDGE,"E55"),sQuery(id+"F4.wireOp",EDGE,"E56"),sQuery(id+"F4.wireOp",EDGE,"E57"),sQuery(id+"F4.wireOp",EDGE,"E58"),sQuery(id+"F4.wireOp",EDGE,"E59.MirrorCS"),sQuery(id+"F4.wireOp",EDGE,"E60.MirrorCS"),sQuery(id+"F4.wireOp",EDGE,"E61.MirrorCS"),sQuery(id+"F4.wireOp",EDGE,"E62.MirrorCS"),sQuery(id+"F4.wireOp",EDGE,"E63.MirrorCS")])],"isStart":false})]})],"blendedInto":[makeQuery(id+"F5.boolean.opBoolean","MERGE",FACE,{"derivedFrom":[makeQuery(id+"F3.opExtrude","CAP_FACE",FACE,{"disambiguationData":[OSD([sQuery(id+"F2.wireOp",EDGE,"E26"),sQuery(id+"F2.wireOp",EDGE,"E27"),sQuery(id+"F2.wireOp",EDGE,"E28"),sQuery(id+"F2.wireOp",EDGE,"E29"),sQuery(id+"F2.wireOp",EDGE,"E30"),sQuery(id+"F2.wireOp",EDGE,"E31"),sQuery(id+"F2.wireOp",EDGE,"E32"),sQuery(id+"F2.wireOp",EDGE,"E33"),sQuery(id+"F2.wireOp",EDGE,"E34"),sQuery(id+"F2.wireOp",EDGE,"E35"),sQuery(id+"F2.wireOp",EDGE,"E36"),sQuery(id+"F2.wireOp",EDGE,"E37"),sQuery(id+"F2.wireOp",EDGE,"E38"),sQuery(id+"F2.wireOp",EDGE,"E39"),sQuery(id+"F2.wireOp",EDGE,"E40.MirrorCS"),sQuery(id+"F2.wireOp",EDGE,"E41.MirrorCS"),subQ0,sQuery(id+"F2.wireOp",EDGE,"E43.MirrorCS"),sQuery(id+"F2.wireOp",EDGE,"E44.MirrorCS"),sQuery(id+"F2.wireOp",EDGE,"E45.MirrorCS"),sQuery(id+"F2.wireOp",EDGE,"E46.MirrorCS"),sQuery(id+"F2.wireOp",EDGE,"E47.MirrorCS"),sQuery(id+"F2.wireOp",EDGE,"E48.MirrorCS"),sQuery(id+"F2.wireOp",EDGE,"E49.MirrorCS"),sQuery(id+"F2.wireOp",EDGE,"E50.MirrorCS"),sQuery(id+"F2.wireOp",EDGE,"E51.MirrorCS"),sQuery(id+"F2.wireOp",EDGE,"E52.MirrorCS"),sQuery(id+"F2.wireOp",EDGE,"E53.MirrorCS")])],"isStart":false}),makeQuery(id+"F5.opExtrude","CAP_FACE",FACE,{"disambiguationData":[OSD([sQuery(id+"F4.wireOp",EDGE,"E54"),sQuery(id+"F4.wireOp",EDGE,"E55"),sQuery(id+"F4.wireOp",EDGE,"E56"),sQuery(id+"F4.wireOp",EDGE,"E57"),sQuery(id+"F4.wireOp",EDGE,"E58"),sQuery(id+"F4.wireOp",EDGE,"E59.MirrorCS"),sQuery(id+"F4.wireOp",EDGE,"E60.MirrorCS"),sQuery(id+"F4.wireOp",EDGE,"E61.MirrorCS"),sQuery(id+"F4.wireOp",EDGE,"E62.MirrorCS"),sQuery(id+"F4.wireOp",EDGE,"E63.MirrorCS")])],"isStart":false})]})]});}
            var Q9;
            {var subQ0=sQuery(id+"F2.wireOp",EDGE,"E53.MirrorCS");Q9=makeQuery(id+"F24.opChamfer","BLEND_EDGE",EDGE,{"blendedFrom":[makeQuery(id+"F3.opExtrude","CAP_EDGE",EDGE,{"disambiguationData":[OSD([subQ0])],"isStart":false}),makeQuery(id+"F5.boolean.opBoolean","MERGE",FACE,{"derivedFrom":[makeQuery(id+"F3.opExtrude","CAP_FACE",FACE,{"disambiguationData":[OSD([sQuery(id+"F2.wireOp",EDGE,"E26"),sQuery(id+"F2.wireOp",EDGE,"E27"),sQuery(id+"F2.wireOp",EDGE,"E28"),sQuery(id+"F2.wireOp",EDGE,"E29"),sQuery(id+"F2.wireOp",EDGE,"E30"),sQuery(id+"F2.wireOp",EDGE,"E31"),sQuery(id+"F2.wireOp",EDGE,"E32"),sQuery(id+"F2.wireOp",EDGE,"E33"),sQuery(id+"F2.wireOp",EDGE,"E34"),sQuery(id+"F2.wireOp",EDGE,"E35"),sQuery(id+"F2.wireOp",EDGE,"E36"),sQuery(id+"F2.wireOp",EDGE,"E37"),sQuery(id+"F2.wireOp",EDGE,"E38"),sQuery(id+"F2.wireOp",EDGE,"E39"),sQuery(id+"F2.wireOp",EDGE,"E40.MirrorCS"),sQuery(id+"F2.wireOp",EDGE,"E41.MirrorCS"),sQuery(id+"F2.wireOp",EDGE,"E42.MirrorCS"),sQuery(id+"F2.wireOp",EDGE,"E43.MirrorCS"),sQuery(id+"F2.wireOp",EDGE,"E44.MirrorCS"),sQuery(id+"F2.wireOp",EDGE,"E45.MirrorCS"),sQuery(id+"F2.wireOp",EDGE,"E46.MirrorCS"),sQuery(id+"F2.wireOp",EDGE,"E47.MirrorCS"),sQuery(id+"F2.wireOp",EDGE,"E48.MirrorCS"),sQuery(id+"F2.wireOp",EDGE,"E49.MirrorCS"),sQuery(id+"F2.wireOp",EDGE,"E50.MirrorCS"),sQuery(id+"F2.wireOp",EDGE,"E51.MirrorCS"),sQuery(id+"F2.wireOp",EDGE,"E52.MirrorCS"),subQ0])],"isStart":false}),makeQuery(id+"F5.opExtrude","CAP_FACE",FACE,{"disambiguationData":[OSD([sQuery(id+"F4.wireOp",EDGE,"E54"),sQuery(id+"F4.wireOp",EDGE,"E55"),sQuery(id+"F4.wireOp",EDGE,"E56"),sQuery(id+"F4.wireOp",EDGE,"E57"),sQuery(id+"F4.wireOp",EDGE,"E58"),sQuery(id+"F4.wireOp",EDGE,"E59.MirrorCS"),sQuery(id+"F4.wireOp",EDGE,"E60.MirrorCS"),sQuery(id+"F4.wireOp",EDGE,"E61.MirrorCS"),sQuery(id+"F4.wireOp",EDGE,"E62.MirrorCS"),sQuery(id+"F4.wireOp",EDGE,"E63.MirrorCS")])],"isStart":false})]})],"blendedInto":[makeQuery(id+"F5.boolean.opBoolean","MERGE",FACE,{"derivedFrom":[makeQuery(id+"F3.opExtrude","CAP_FACE",FACE,{"disambiguationData":[OSD([sQuery(id+"F2.wireOp",EDGE,"E26"),sQuery(id+"F2.wireOp",EDGE,"E27"),sQuery(id+"F2.wireOp",EDGE,"E28"),sQuery(id+"F2.wireOp",EDGE,"E29"),sQuery(id+"F2.wireOp",EDGE,"E30"),sQuery(id+"F2.wireOp",EDGE,"E31"),sQuery(id+"F2.wireOp",EDGE,"E32"),sQuery(id+"F2.wireOp",EDGE,"E33"),sQuery(id+"F2.wireOp",EDGE,"E34"),sQuery(id+"F2.wireOp",EDGE,"E35"),sQuery(id+"F2.wireOp",EDGE,"E36"),sQuery(id+"F2.wireOp",EDGE,"E37"),sQuery(id+"F2.wireOp",EDGE,"E38"),sQuery(id+"F2.wireOp",EDGE,"E39"),sQuery(id+"F2.wireOp",EDGE,"E40.MirrorCS"),sQuery(id+"F2.wireOp",EDGE,"E41.MirrorCS"),sQuery(id+"F2.wireOp",EDGE,"E42.MirrorCS"),sQuery(id+"F2.wireOp",EDGE,"E43.MirrorCS"),sQuery(id+"F2.wireOp",EDGE,"E44.MirrorCS"),sQuery(id+"F2.wireOp",EDGE,"E45.MirrorCS"),sQuery(id+"F2.wireOp",EDGE,"E46.MirrorCS"),sQuery(id+"F2.wireOp",EDGE,"E47.MirrorCS"),sQuery(id+"F2.wireOp",EDGE,"E48.MirrorCS"),sQuery(id+"F2.wireOp",EDGE,"E49.MirrorCS"),sQuery(id+"F2.wireOp",EDGE,"E50.MirrorCS"),sQuery(id+"F2.wireOp",EDGE,"E51.MirrorCS"),sQuery(id+"F2.wireOp",EDGE,"E52.MirrorCS"),subQ0])],"isStart":false}),makeQuery(id+"F5.opExtrude","CAP_FACE",FACE,{"disambiguationData":[OSD([sQuery(id+"F4.wireOp",EDGE,"E54"),sQuery(id+"F4.wireOp",EDGE,"E55"),sQuery(id+"F4.wireOp",EDGE,"E56"),sQuery(id+"F4.wireOp",EDGE,"E57"),sQuery(id+"F4.wireOp",EDGE,"E58"),sQuery(id+"F4.wireOp",EDGE,"E59.MirrorCS"),sQuery(id+"F4.wireOp",EDGE,"E60.MirrorCS"),sQuery(id+"F4.wireOp",EDGE,"E61.MirrorCS"),sQuery(id+"F4.wireOp",EDGE,"E62.MirrorCS"),sQuery(id+"F4.wireOp",EDGE,"E63.MirrorCS")])],"isStart":false})]})]});}
            var Q10;
            {var subQ0=sQuery(id+"F4.wireOp",EDGE,"E60.MirrorCS");var subQ1=makeQuery(id+"F5.opExtrude","CAP_FACE",FACE,{"disambiguationData":[OSD([sQuery(id+"F4.wireOp",EDGE,"E54"),sQuery(id+"F4.wireOp",EDGE,"E55"),sQuery(id+"F4.wireOp",EDGE,"E56"),sQuery(id+"F4.wireOp",EDGE,"E57"),sQuery(id+"F4.wireOp",EDGE,"E58"),sQuery(id+"F4.wireOp",EDGE,"E59.MirrorCS"),subQ0,sQuery(id+"F4.wireOp",EDGE,"E61.MirrorCS"),sQuery(id+"F4.wireOp",EDGE,"E62.MirrorCS"),sQuery(id+"F4.wireOp",EDGE,"E63.MirrorCS")])],"isStart":false});var subQ2=sQuery(id+"F2.wireOp",EDGE,"E53.MirrorCS");var subQ3=sQuery(id+"F2.wireOp",EDGE,"E48.MirrorCS");var subQ4=makeQuery(id+"F3.opExtrude","CAP_FACE",FACE,{"disambiguationData":[OSD([sQuery(id+"F2.wireOp",EDGE,"E26"),sQuery(id+"F2.wireOp",EDGE,"E27"),sQuery(id+"F2.wireOp",EDGE,"E28"),sQuery(id+"F2.wireOp",EDGE,"E29"),sQuery(id+"F2.wireOp",EDGE,"E30"),sQuery(id+"F2.wireOp",EDGE,"E31"),sQuery(id+"F2.wireOp",EDGE,"E32"),sQuery(id+"F2.wireOp",EDGE,"E33"),sQuery(id+"F2.wireOp",EDGE,"E34"),sQuery(id+"F2.wireOp",EDGE,"E35"),sQuery(id+"F2.wireOp",EDGE,"E36"),sQuery(id+"F2.wireOp",EDGE,"E37"),sQuery(id+"F2.wireOp",EDGE,"E38"),sQuery(id+"F2.wireOp",EDGE,"E39"),sQuery(id+"F2.wireOp",EDGE,"E40.MirrorCS"),sQuery(id+"F2.wireOp",EDGE,"E41.MirrorCS"),sQuery(id+"F2.wireOp",EDGE,"E42.MirrorCS"),sQuery(id+"F2.wireOp",EDGE,"E43.MirrorCS"),sQuery(id+"F2.wireOp",EDGE,"E44.MirrorCS"),sQuery(id+"F2.wireOp",EDGE,"E45.MirrorCS"),sQuery(id+"F2.wireOp",EDGE,"E46.MirrorCS"),sQuery(id+"F2.wireOp",EDGE,"E47.MirrorCS"),subQ3,sQuery(id+"F2.wireOp",EDGE,"E49.MirrorCS"),sQuery(id+"F2.wireOp",EDGE,"E50.MirrorCS"),sQuery(id+"F2.wireOp",EDGE,"E51.MirrorCS"),sQuery(id+"F2.wireOp",EDGE,"E52.MirrorCS"),subQ2])],"isStart":false});Q10=makeQuery(id+"F24.opChamfer","BLEND_EDGE",EDGE,{"blendedFrom":[makeQuery(id+"F5.boolean.opBoolean","SPLIT",EDGE,{"disambiguationData":[TD([makeQuery(id+"F3.opExtrude","SWEPT_FACE",FACE,{"disambiguationData":[OSD([subQ2])]})])],"derivedFrom":makeQuery(id+"F3.opExtrude","CAP_EDGE",EDGE,{"disambiguationData":[OSD([subQ3])],"isStart":false})}),makeQuery(id+"F5.boolean.opBoolean","MERGE",FACE,{"derivedFrom":[subQ4,subQ1]})],"blendedInto":[makeQuery(id+"F5.boolean.opBoolean","MERGE",FACE,{"derivedFrom":[subQ4,subQ1]})]});}
            var Q11;
            {var subQ0=sQuery(id+"F4.wireOp",EDGE,"E63.MirrorCS");Q11=makeQuery(id+"F24.opChamfer","BLEND_EDGE",EDGE,{"blendedFrom":[makeQuery(id+"F5.opExtrude","CAP_EDGE",EDGE,{"disambiguationData":[OSD([subQ0])],"isStart":false}),makeQuery(id+"F5.boolean.opBoolean","MERGE",FACE,{"derivedFrom":[makeQuery(id+"F3.opExtrude","CAP_FACE",FACE,{"disambiguationData":[OSD([sQuery(id+"F2.wireOp",EDGE,"E26"),sQuery(id+"F2.wireOp",EDGE,"E27"),sQuery(id+"F2.wireOp",EDGE,"E28"),sQuery(id+"F2.wireOp",EDGE,"E29"),sQuery(id+"F2.wireOp",EDGE,"E30"),sQuery(id+"F2.wireOp",EDGE,"E31"),sQuery(id+"F2.wireOp",EDGE,"E32"),sQuery(id+"F2.wireOp",EDGE,"E33"),sQuery(id+"F2.wireOp",EDGE,"E34"),sQuery(id+"F2.wireOp",EDGE,"E35"),sQuery(id+"F2.wireOp",EDGE,"E36"),sQuery(id+"F2.wireOp",EDGE,"E37"),sQuery(id+"F2.wireOp",EDGE,"E38"),sQuery(id+"F2.wireOp",EDGE,"E39"),sQuery(id+"F2.wireOp",EDGE,"E40.MirrorCS"),sQuery(id+"F2.wireOp",EDGE,"E41.MirrorCS"),sQuery(id+"F2.wireOp",EDGE,"E42.MirrorCS"),sQuery(id+"F2.wireOp",EDGE,"E43.MirrorCS"),sQuery(id+"F2.wireOp",EDGE,"E44.MirrorCS"),sQuery(id+"F2.wireOp",EDGE,"E45.MirrorCS"),sQuery(id+"F2.wireOp",EDGE,"E46.MirrorCS"),sQuery(id+"F2.wireOp",EDGE,"E47.MirrorCS"),sQuery(id+"F2.wireOp",EDGE,"E48.MirrorCS"),sQuery(id+"F2.wireOp",EDGE,"E49.MirrorCS"),sQuery(id+"F2.wireOp",EDGE,"E50.MirrorCS"),sQuery(id+"F2.wireOp",EDGE,"E51.MirrorCS"),sQuery(id+"F2.wireOp",EDGE,"E52.MirrorCS"),sQuery(id+"F2.wireOp",EDGE,"E53.MirrorCS")])],"isStart":false}),makeQuery(id+"F5.opExtrude","CAP_FACE",FACE,{"disambiguationData":[OSD([sQuery(id+"F4.wireOp",EDGE,"E54"),sQuery(id+"F4.wireOp",EDGE,"E55"),sQuery(id+"F4.wireOp",EDGE,"E56"),sQuery(id+"F4.wireOp",EDGE,"E57"),sQuery(id+"F4.wireOp",EDGE,"E58"),sQuery(id+"F4.wireOp",EDGE,"E59.MirrorCS"),sQuery(id+"F4.wireOp",EDGE,"E60.MirrorCS"),sQuery(id+"F4.wireOp",EDGE,"E61.MirrorCS"),sQuery(id+"F4.wireOp",EDGE,"E62.MirrorCS"),subQ0])],"isStart":false})]})],"blendedInto":[makeQuery(id+"F5.boolean.opBoolean","MERGE",FACE,{"derivedFrom":[makeQuery(id+"F3.opExtrude","CAP_FACE",FACE,{"disambiguationData":[OSD([sQuery(id+"F2.wireOp",EDGE,"E26"),sQuery(id+"F2.wireOp",EDGE,"E27"),sQuery(id+"F2.wireOp",EDGE,"E28"),sQuery(id+"F2.wireOp",EDGE,"E29"),sQuery(id+"F2.wireOp",EDGE,"E30"),sQuery(id+"F2.wireOp",EDGE,"E31"),sQuery(id+"F2.wireOp",EDGE,"E32"),sQuery(id+"F2.wireOp",EDGE,"E33"),sQuery(id+"F2.wireOp",EDGE,"E34"),sQuery(id+"F2.wireOp",EDGE,"E35"),sQuery(id+"F2.wireOp",EDGE,"E36"),sQuery(id+"F2.wireOp",EDGE,"E37"),sQuery(id+"F2.wireOp",EDGE,"E38"),sQuery(id+"F2.wireOp",EDGE,"E39"),sQuery(id+"F2.wireOp",EDGE,"E40.MirrorCS"),sQuery(id+"F2.wireOp",EDGE,"E41.MirrorCS"),sQuery(id+"F2.wireOp",EDGE,"E42.MirrorCS"),sQuery(id+"F2.wireOp",EDGE,"E43.MirrorCS"),sQuery(id+"F2.wireOp",EDGE,"E44.MirrorCS"),sQuery(id+"F2.wireOp",EDGE,"E45.MirrorCS"),sQuery(id+"F2.wireOp",EDGE,"E46.MirrorCS"),sQuery(id+"F2.wireOp",EDGE,"E47.MirrorCS"),sQuery(id+"F2.wireOp",EDGE,"E48.MirrorCS"),sQuery(id+"F2.wireOp",EDGE,"E49.MirrorCS"),sQuery(id+"F2.wireOp",EDGE,"E50.MirrorCS"),sQuery(id+"F2.wireOp",EDGE,"E51.MirrorCS"),sQuery(id+"F2.wireOp",EDGE,"E52.MirrorCS"),sQuery(id+"F2.wireOp",EDGE,"E53.MirrorCS")])],"isStart":false}),makeQuery(id+"F5.opExtrude","CAP_FACE",FACE,{"disambiguationData":[OSD([sQuery(id+"F4.wireOp",EDGE,"E54"),sQuery(id+"F4.wireOp",EDGE,"E55"),sQuery(id+"F4.wireOp",EDGE,"E56"),sQuery(id+"F4.wireOp",EDGE,"E57"),sQuery(id+"F4.wireOp",EDGE,"E58"),sQuery(id+"F4.wireOp",EDGE,"E59.MirrorCS"),sQuery(id+"F4.wireOp",EDGE,"E60.MirrorCS"),sQuery(id+"F4.wireOp",EDGE,"E61.MirrorCS"),sQuery(id+"F4.wireOp",EDGE,"E62.MirrorCS"),subQ0])],"isStart":false})]})]});}
            var Q12;
            {var subQ0=sQuery(id+"F4.wireOp",EDGE,"E60.MirrorCS");Q12=makeQuery(id+"F24.opChamfer","BLEND_EDGE",EDGE,{"blendedFrom":[makeQuery(id+"F5.opExtrude","CAP_EDGE",EDGE,{"disambiguationData":[OSD([subQ0])],"isStart":false}),makeQuery(id+"F5.boolean.opBoolean","MERGE",FACE,{"derivedFrom":[makeQuery(id+"F3.opExtrude","CAP_FACE",FACE,{"disambiguationData":[OSD([sQuery(id+"F2.wireOp",EDGE,"E26"),sQuery(id+"F2.wireOp",EDGE,"E27"),sQuery(id+"F2.wireOp",EDGE,"E28"),sQuery(id+"F2.wireOp",EDGE,"E29"),sQuery(id+"F2.wireOp",EDGE,"E30"),sQuery(id+"F2.wireOp",EDGE,"E31"),sQuery(id+"F2.wireOp",EDGE,"E32"),sQuery(id+"F2.wireOp",EDGE,"E33"),sQuery(id+"F2.wireOp",EDGE,"E34"),sQuery(id+"F2.wireOp",EDGE,"E35"),sQuery(id+"F2.wireOp",EDGE,"E36"),sQuery(id+"F2.wireOp",EDGE,"E37"),sQuery(id+"F2.wireOp",EDGE,"E38"),sQuery(id+"F2.wireOp",EDGE,"E39"),sQuery(id+"F2.wireOp",EDGE,"E40.MirrorCS"),sQuery(id+"F2.wireOp",EDGE,"E41.MirrorCS"),sQuery(id+"F2.wireOp",EDGE,"E42.MirrorCS"),sQuery(id+"F2.wireOp",EDGE,"E43.MirrorCS"),sQuery(id+"F2.wireOp",EDGE,"E44.MirrorCS"),sQuery(id+"F2.wireOp",EDGE,"E45.MirrorCS"),sQuery(id+"F2.wireOp",EDGE,"E46.MirrorCS"),sQuery(id+"F2.wireOp",EDGE,"E47.MirrorCS"),sQuery(id+"F2.wireOp",EDGE,"E48.MirrorCS"),sQuery(id+"F2.wireOp",EDGE,"E49.MirrorCS"),sQuery(id+"F2.wireOp",EDGE,"E50.MirrorCS"),sQuery(id+"F2.wireOp",EDGE,"E51.MirrorCS"),sQuery(id+"F2.wireOp",EDGE,"E52.MirrorCS"),sQuery(id+"F2.wireOp",EDGE,"E53.MirrorCS")])],"isStart":false}),makeQuery(id+"F5.opExtrude","CAP_FACE",FACE,{"disambiguationData":[OSD([sQuery(id+"F4.wireOp",EDGE,"E54"),sQuery(id+"F4.wireOp",EDGE,"E55"),sQuery(id+"F4.wireOp",EDGE,"E56"),sQuery(id+"F4.wireOp",EDGE,"E57"),sQuery(id+"F4.wireOp",EDGE,"E58"),sQuery(id+"F4.wireOp",EDGE,"E59.MirrorCS"),subQ0,sQuery(id+"F4.wireOp",EDGE,"E61.MirrorCS"),sQuery(id+"F4.wireOp",EDGE,"E62.MirrorCS"),sQuery(id+"F4.wireOp",EDGE,"E63.MirrorCS")])],"isStart":false})]})],"blendedInto":[makeQuery(id+"F5.boolean.opBoolean","MERGE",FACE,{"derivedFrom":[makeQuery(id+"F3.opExtrude","CAP_FACE",FACE,{"disambiguationData":[OSD([sQuery(id+"F2.wireOp",EDGE,"E26"),sQuery(id+"F2.wireOp",EDGE,"E27"),sQuery(id+"F2.wireOp",EDGE,"E28"),sQuery(id+"F2.wireOp",EDGE,"E29"),sQuery(id+"F2.wireOp",EDGE,"E30"),sQuery(id+"F2.wireOp",EDGE,"E31"),sQuery(id+"F2.wireOp",EDGE,"E32"),sQuery(id+"F2.wireOp",EDGE,"E33"),sQuery(id+"F2.wireOp",EDGE,"E34"),sQuery(id+"F2.wireOp",EDGE,"E35"),sQuery(id+"F2.wireOp",EDGE,"E36"),sQuery(id+"F2.wireOp",EDGE,"E37"),sQuery(id+"F2.wireOp",EDGE,"E38"),sQuery(id+"F2.wireOp",EDGE,"E39"),sQuery(id+"F2.wireOp",EDGE,"E40.MirrorCS"),sQuery(id+"F2.wireOp",EDGE,"E41.MirrorCS"),sQuery(id+"F2.wireOp",EDGE,"E42.MirrorCS"),sQuery(id+"F2.wireOp",EDGE,"E43.MirrorCS"),sQuery(id+"F2.wireOp",EDGE,"E44.MirrorCS"),sQuery(id+"F2.wireOp",EDGE,"E45.MirrorCS"),sQuery(id+"F2.wireOp",EDGE,"E46.MirrorCS"),sQuery(id+"F2.wireOp",EDGE,"E47.MirrorCS"),sQuery(id+"F2.wireOp",EDGE,"E48.MirrorCS"),sQuery(id+"F2.wireOp",EDGE,"E49.MirrorCS"),sQuery(id+"F2.wireOp",EDGE,"E50.MirrorCS"),sQuery(id+"F2.wireOp",EDGE,"E51.MirrorCS"),sQuery(id+"F2.wireOp",EDGE,"E52.MirrorCS"),sQuery(id+"F2.wireOp",EDGE,"E53.MirrorCS")])],"isStart":false}),makeQuery(id+"F5.opExtrude","CAP_FACE",FACE,{"disambiguationData":[OSD([sQuery(id+"F4.wireOp",EDGE,"E54"),sQuery(id+"F4.wireOp",EDGE,"E55"),sQuery(id+"F4.wireOp",EDGE,"E56"),sQuery(id+"F4.wireOp",EDGE,"E57"),sQuery(id+"F4.wireOp",EDGE,"E58"),sQuery(id+"F4.wireOp",EDGE,"E59.MirrorCS"),subQ0,sQuery(id+"F4.wireOp",EDGE,"E61.MirrorCS"),sQuery(id+"F4.wireOp",EDGE,"E62.MirrorCS"),sQuery(id+"F4.wireOp",EDGE,"E63.MirrorCS")])],"isStart":false})]})]});}
            var Q13;
            {var subQ0=sQuery(id+"F4.wireOp",EDGE,"E57");Q13=makeQuery(id+"F24.opChamfer","BLEND_EDGE",EDGE,{"blendedFrom":[makeQuery(id+"F5.opExtrude","CAP_EDGE",EDGE,{"disambiguationData":[OSD([subQ0])],"isStart":false}),makeQuery(id+"F5.boolean.opBoolean","MERGE",FACE,{"derivedFrom":[makeQuery(id+"F3.opExtrude","CAP_FACE",FACE,{"disambiguationData":[OSD([sQuery(id+"F2.wireOp",EDGE,"E26"),sQuery(id+"F2.wireOp",EDGE,"E27"),sQuery(id+"F2.wireOp",EDGE,"E28"),sQuery(id+"F2.wireOp",EDGE,"E29"),sQuery(id+"F2.wireOp",EDGE,"E30"),sQuery(id+"F2.wireOp",EDGE,"E31"),sQuery(id+"F2.wireOp",EDGE,"E32"),sQuery(id+"F2.wireOp",EDGE,"E33"),sQuery(id+"F2.wireOp",EDGE,"E34"),sQuery(id+"F2.wireOp",EDGE,"E35"),sQuery(id+"F2.wireOp",EDGE,"E36"),sQuery(id+"F2.wireOp",EDGE,"E37"),sQuery(id+"F2.wireOp",EDGE,"E38"),sQuery(id+"F2.wireOp",EDGE,"E39"),sQuery(id+"F2.wireOp",EDGE,"E40.MirrorCS"),sQuery(id+"F2.wireOp",EDGE,"E41.MirrorCS"),sQuery(id+"F2.wireOp",EDGE,"E42.MirrorCS"),sQuery(id+"F2.wireOp",EDGE,"E43.MirrorCS"),sQuery(id+"F2.wireOp",EDGE,"E44.MirrorCS"),sQuery(id+"F2.wireOp",EDGE,"E45.MirrorCS"),sQuery(id+"F2.wireOp",EDGE,"E46.MirrorCS"),sQuery(id+"F2.wireOp",EDGE,"E47.MirrorCS"),sQuery(id+"F2.wireOp",EDGE,"E48.MirrorCS"),sQuery(id+"F2.wireOp",EDGE,"E49.MirrorCS"),sQuery(id+"F2.wireOp",EDGE,"E50.MirrorCS"),sQuery(id+"F2.wireOp",EDGE,"E51.MirrorCS"),sQuery(id+"F2.wireOp",EDGE,"E52.MirrorCS"),sQuery(id+"F2.wireOp",EDGE,"E53.MirrorCS")])],"isStart":false}),makeQuery(id+"F5.opExtrude","CAP_FACE",FACE,{"disambiguationData":[OSD([sQuery(id+"F4.wireOp",EDGE,"E54"),sQuery(id+"F4.wireOp",EDGE,"E55"),sQuery(id+"F4.wireOp",EDGE,"E56"),subQ0,sQuery(id+"F4.wireOp",EDGE,"E58"),sQuery(id+"F4.wireOp",EDGE,"E59.MirrorCS"),sQuery(id+"F4.wireOp",EDGE,"E60.MirrorCS"),sQuery(id+"F4.wireOp",EDGE,"E61.MirrorCS"),sQuery(id+"F4.wireOp",EDGE,"E62.MirrorCS"),sQuery(id+"F4.wireOp",EDGE,"E63.MirrorCS")])],"isStart":false})]})],"blendedInto":[makeQuery(id+"F5.boolean.opBoolean","MERGE",FACE,{"derivedFrom":[makeQuery(id+"F3.opExtrude","CAP_FACE",FACE,{"disambiguationData":[OSD([sQuery(id+"F2.wireOp",EDGE,"E26"),sQuery(id+"F2.wireOp",EDGE,"E27"),sQuery(id+"F2.wireOp",EDGE,"E28"),sQuery(id+"F2.wireOp",EDGE,"E29"),sQuery(id+"F2.wireOp",EDGE,"E30"),sQuery(id+"F2.wireOp",EDGE,"E31"),sQuery(id+"F2.wireOp",EDGE,"E32"),sQuery(id+"F2.wireOp",EDGE,"E33"),sQuery(id+"F2.wireOp",EDGE,"E34"),sQuery(id+"F2.wireOp",EDGE,"E35"),sQuery(id+"F2.wireOp",EDGE,"E36"),sQuery(id+"F2.wireOp",EDGE,"E37"),sQuery(id+"F2.wireOp",EDGE,"E38"),sQuery(id+"F2.wireOp",EDGE,"E39"),sQuery(id+"F2.wireOp",EDGE,"E40.MirrorCS"),sQuery(id+"F2.wireOp",EDGE,"E41.MirrorCS"),sQuery(id+"F2.wireOp",EDGE,"E42.MirrorCS"),sQuery(id+"F2.wireOp",EDGE,"E43.MirrorCS"),sQuery(id+"F2.wireOp",EDGE,"E44.MirrorCS"),sQuery(id+"F2.wireOp",EDGE,"E45.MirrorCS"),sQuery(id+"F2.wireOp",EDGE,"E46.MirrorCS"),sQuery(id+"F2.wireOp",EDGE,"E47.MirrorCS"),sQuery(id+"F2.wireOp",EDGE,"E48.MirrorCS"),sQuery(id+"F2.wireOp",EDGE,"E49.MirrorCS"),sQuery(id+"F2.wireOp",EDGE,"E50.MirrorCS"),sQuery(id+"F2.wireOp",EDGE,"E51.MirrorCS"),sQuery(id+"F2.wireOp",EDGE,"E52.MirrorCS"),sQuery(id+"F2.wireOp",EDGE,"E53.MirrorCS")])],"isStart":false}),makeQuery(id+"F5.opExtrude","CAP_FACE",FACE,{"disambiguationData":[OSD([sQuery(id+"F4.wireOp",EDGE,"E54"),sQuery(id+"F4.wireOp",EDGE,"E55"),sQuery(id+"F4.wireOp",EDGE,"E56"),subQ0,sQuery(id+"F4.wireOp",EDGE,"E58"),sQuery(id+"F4.wireOp",EDGE,"E59.MirrorCS"),sQuery(id+"F4.wireOp",EDGE,"E60.MirrorCS"),sQuery(id+"F4.wireOp",EDGE,"E61.MirrorCS"),sQuery(id+"F4.wireOp",EDGE,"E62.MirrorCS"),sQuery(id+"F4.wireOp",EDGE,"E63.MirrorCS")])],"isStart":false})]})]});}
            chamfer(context, id + "F25", {"entities" : qUnion([Q0, Q1, Q2, Q3, Q4, Q5, Q6, Q7, Q8, Q9, Q10, Q11, Q12, Q13]), "width" : .5 * mm, "tangentPropagation" : true});
        }
        {
            var Q0;
            Q0=makeQuery(id+"F13.opExtrude","CAP_EDGE",EDGE,{"disambiguationData":[OSD([sQuery(id+"F12.wireOp",EDGE,"E101")])],"isStart":false});
            var Q1;
            Q1=makeQuery(id+"F13.opExtrude","CAP_EDGE",EDGE,{"disambiguationData":[OSD([sQuery(id+"F12.wireOp",EDGE,"E103")])],"isStart":false});
            var Q2;
            Q2=makeQuery(id+"F13.opExtrude","CAP_EDGE",EDGE,{"disambiguationData":[OSD([sQuery(id+"F12.wireOp",EDGE,"E104")])],"isStart":false});
            var Q3;
            Q3=makeQuery(id+"F13.opExtrude","CAP_EDGE",EDGE,{"disambiguationData":[OSD([sQuery(id+"F12.wireOp",EDGE,"E105.MirrorCS")])],"isStart":false});
            var Q4;
            Q4=makeQuery(id+"F13.opExtrude","CAP_EDGE",EDGE,{"disambiguationData":[OSD([sQuery(id+"F12.wireOp",EDGE,"E106.MirrorCS")])],"isStart":false});
            var Q5;
            Q5=makeQuery(id+"F13.opExtrude","CAP_EDGE",EDGE,{"disambiguationData":[OSD([sQuery(id+"F12.wireOp",EDGE,"E108.MirrorCS")])],"isStart":false});
            var Q6;
            Q6=makeQuery(id+"F13.opExtrude","CAP_EDGE",EDGE,{"disambiguationData":[OSD([sQuery(id+"F12.wireOp",EDGE,"E102")])],"isStart":false});
            var Q7;
            Q7=makeQuery(id+"F13.opExtrude","CAP_EDGE",EDGE,{"disambiguationData":[OSD([sQuery(id+"F12.wireOp",EDGE,"E100")])],"isStart":false});
            var Q8;
            Q8=makeQuery(id+"F13.opExtrude","CAP_EDGE",EDGE,{"disambiguationData":[OSD([sQuery(id+"F12.wireOp",EDGE,"E109.MirrorCS")])],"isStart":false});
            var Q9;
            Q9=makeQuery(id+"F13.opExtrude","CAP_EDGE",EDGE,{"disambiguationData":[OSD([sQuery(id+"F12.wireOp",EDGE,"E107.MirrorCS")])],"isStart":false});
            chamfer(context, id + "F26", {"entities" : qUnion([Q0, Q1, Q2, Q3, Q4, Q5, Q6, Q7, Q8, Q9]), "width" : 1 * mm, "tangentPropagation" : true});
        }
        {
            var Q0;
            Q0=makeQuery(id+"F15.opExtrude","CAP_FACE",FACE,{"disambiguationData":[OSD([sQuery(id+"F14.wireOp",EDGE,"E110"),sQuery(id+"F14.wireOp",EDGE,"E111"),sQuery(id+"F14.wireOp",EDGE,"E112"),sQuery(id+"F14.wireOp",EDGE,"E113"),sQuery(id+"F14.wireOp",EDGE,"E114"),sQuery(id+"F14.wireOp",EDGE,"E115"),sQuery(id+"F14.wireOp",EDGE,"E116"),sQuery(id+"F14.wireOp",EDGE,"E117"),sQuery(id+"F14.wireOp",EDGE,"E118"),sQuery(id+"F14.wireOp",EDGE,"E119"),sQuery(id+"F14.wireOp",EDGE,"E120"),sQuery(id+"F14.wireOp",EDGE,"E121"),sQuery(id+"F14.wireOp",EDGE,"E122"),sQuery(id+"F14.wireOp",EDGE,"E123"),sQuery(id+"F14.wireOp",EDGE,"E124"),sQuery(id+"F14.wireOp",EDGE,"E125"),sQuery(id+"F14.wireOp",EDGE,"E126"),sQuery(id+"F14.wireOp",EDGE,"E127.MirrorCS"),sQuery(id+"F14.wireOp",EDGE,"E128.MirrorCS"),sQuery(id+"F14.wireOp",EDGE,"E129.MirrorCS"),sQuery(id+"F14.wireOp",EDGE,"E130.MirrorCS"),sQuery(id+"F14.wireOp",EDGE,"E131.MirrorCS"),sQuery(id+"F14.wireOp",EDGE,"E132.MirrorCS"),sQuery(id+"F14.wireOp",EDGE,"E133.MirrorCS"),sQuery(id+"F14.wireOp",EDGE,"E134.MirrorCS"),sQuery(id+"F14.wireOp",EDGE,"E135.MirrorCS"),sQuery(id+"F14.wireOp",EDGE,"E136.MirrorCS"),sQuery(id+"F14.wireOp",EDGE,"E137.MirrorCS"),sQuery(id+"F14.wireOp",EDGE,"E138.MirrorCS"),sQuery(id+"F14.wireOp",EDGE,"E139.MirrorCS"),sQuery(id+"F14.wireOp",EDGE,"E140.MirrorCS"),sQuery(id+"F14.wireOp",EDGE,"E141.MirrorCS"),sQuery(id+"F14.wireOp",EDGE,"E142.MirrorCS"),sQuery(id+"F14.wireOp",EDGE,"E143.MirrorCS")])],"isStart":false});
            var sketch = newSketch(context, id + "F27", { "sketchPlane" : qUnion([Q0])});
            skSolve(sketch);
        }
        {
            var Q0;
            Q0=makeQuery(id+"F15.opExtrude","CAP_FACE",FACE,{"disambiguationData":[OSD([sQuery(id+"F14.wireOp",EDGE,"E110"),sQuery(id+"F14.wireOp",EDGE,"E111"),sQuery(id+"F14.wireOp",EDGE,"E112"),sQuery(id+"F14.wireOp",EDGE,"E113"),sQuery(id+"F14.wireOp",EDGE,"E114"),sQuery(id+"F14.wireOp",EDGE,"E115"),sQuery(id+"F14.wireOp",EDGE,"E116"),sQuery(id+"F14.wireOp",EDGE,"E117"),sQuery(id+"F14.wireOp",EDGE,"E118"),sQuery(id+"F14.wireOp",EDGE,"E119"),sQuery(id+"F14.wireOp",EDGE,"E120"),sQuery(id+"F14.wireOp",EDGE,"E121"),sQuery(id+"F14.wireOp",EDGE,"E122"),sQuery(id+"F14.wireOp",EDGE,"E123"),sQuery(id+"F14.wireOp",EDGE,"E124"),sQuery(id+"F14.wireOp",EDGE,"E125"),sQuery(id+"F14.wireOp",EDGE,"E126"),sQuery(id+"F14.wireOp",EDGE,"E127.MirrorCS"),sQuery(id+"F14.wireOp",EDGE,"E128.MirrorCS"),sQuery(id+"F14.wireOp",EDGE,"E129.MirrorCS"),sQuery(id+"F14.wireOp",EDGE,"E130.MirrorCS"),sQuery(id+"F14.wireOp",EDGE,"E131.MirrorCS"),sQuery(id+"F14.wireOp",EDGE,"E132.MirrorCS"),sQuery(id+"F14.wireOp",EDGE,"E133.MirrorCS"),sQuery(id+"F14.wireOp",EDGE,"E134.MirrorCS"),sQuery(id+"F14.wireOp",EDGE,"E135.MirrorCS"),sQuery(id+"F14.wireOp",EDGE,"E136.MirrorCS"),sQuery(id+"F14.wireOp",EDGE,"E137.MirrorCS"),sQuery(id+"F14.wireOp",EDGE,"E138.MirrorCS"),sQuery(id+"F14.wireOp",EDGE,"E139.MirrorCS"),sQuery(id+"F14.wireOp",EDGE,"E140.MirrorCS"),sQuery(id+"F14.wireOp",EDGE,"E141.MirrorCS"),sQuery(id+"F14.wireOp",EDGE,"E142.MirrorCS"),sQuery(id+"F14.wireOp",EDGE,"E143.MirrorCS")])],"isStart":false});
            var sketch = newSketch(context, id + "F28", { "sketchPlane" : qUnion([Q0])});
            skLineSegment(sketch, "E196", {"start": v(0, -18.24) * mm, "end": v(7.36, -29.62) * mm});
            skLineSegment(sketch, "E197", {"start": v(7.36, -29.62) * mm, "end": v(7.36, -29.62) * mm});
            skLineSegment(sketch, "E198", {"start": v(15.61, -28.48) * mm, "end": v(67.36, -4.9) * mm});
            skLineSegment(sketch, "E199", {"start": v(67.36, -4.9) * mm, "end": v(67.36, -12.43) * mm});
            skLineSegment(sketch, "E200", {"start": v(67.36, -12.43) * mm, "end": v(15.81, -37.08) * mm});
            skLineSegment(sketch, "E201", {"start": v(15.81, -37.08) * mm, "end": v(12.68, -32.89) * mm});
            skLineSegment(sketch, "E202", {"start": v(12.68, -32.89) * mm, "end": v(9.7, -34.3) * mm});
            skLineSegment(sketch, "E203", {"start": v(9.7, -34.3) * mm, "end": v(12.69, -38.23) * mm});
            skLineSegment(sketch, "E204", {"start": v(12.69, -38.23) * mm, "end": v(12.69, -38.23) * mm});
            skLineSegment(sketch, "E205", {"start": v(0, -48.73) * mm, "end": v(11.87, -38.15) * mm});
            skLineSegment(sketch, "E206", {"start": v(11.87, -38.15) * mm, "end": v(8.77, -34.08) * mm});
            skLineSegment(sketch, "E207", {"start": v(8.77, -34.08) * mm, "end": v(12.86, -32.13) * mm});
            skLineSegment(sketch, "E208", {"start": v(12.86, -32.13) * mm, "end": v(16, -36.32) * mm});
            skLineSegment(sketch, "E209", {"start": v(16, -36.32) * mm, "end": v(66.16, -12.34) * mm});
            skLineSegment(sketch, "E210", {"start": v(66.16, -12.34) * mm, "end": v(66.16, -6.11) * mm});
            skLineSegment(sketch, "E211", {"start": v(66.16, -6.11) * mm, "end": v(15.42, -29.23) * mm});
            skLineSegment(sketch, "E212", {"start": v(7.36, -29.62) * mm, "end": v(10.95, -27.9) * mm});
            skLineSegment(sketch, "E213", {"start": v(10.95, -27.9) * mm, "end": v(0, -8.6) * mm});
            skLineSegment(sketch, "E214", {"start": v(15.42, -29.23) * mm, "end": v(13.18, -26.23) * mm});
            skLineSegment(sketch, "E215", {"start": v(15.61, -28.48) * mm, "end": v(14.1, -26.47) * mm});
            skLineSegment(sketch, "E216", {"start": v(14.1, -26.47) * mm, "end": v(61.26, -5) * mm});
            skLineSegment(sketch, "E217", {"start": v(61.26, -5) * mm, "end": v(60.1, 4) * mm});
            skLineSegment(sketch, "E218", {"start": v(60.1, 4) * mm, "end": v(48.52, 18.4) * mm});
            skLineSegment(sketch, "E219", {"start": v(48.52, 18.4) * mm, "end": v(48.52, 50.9) * mm});
            skLineSegment(sketch, "E220", {"start": v(48.52, 50.9) * mm, "end": v(7.9, 57.48) * mm});
            skLineSegment(sketch, "E221", {"start": v(7.9, 57.48) * mm, "end": v(0, 45.69) * mm});
            skLineSegment(sketch, "E222", {"start": v(13.18, -26.23) * mm, "end": v(60.6, -4.63) * mm});
            skLineSegment(sketch, "E223", {"start": v(60.6, -4.63) * mm, "end": v(59.54, 3.75) * mm});
            skLineSegment(sketch, "E224", {"start": v(59.54, 3.75) * mm, "end": v(47.92, 18.18) * mm});
            skLineSegment(sketch, "E225", {"start": v(47.92, 18.18) * mm, "end": v(47.92, 50.38) * mm});
            skLineSegment(sketch, "E226", {"start": v(47.92, 50.38) * mm, "end": v(8.18, 56.83) * mm});
            skLineSegment(sketch, "E227", {"start": v(8.18, 56.83) * mm, "end": v(0, 44.6) * mm});
            skLineSegment(sketch, "E228", {"start": v(0, -19.35) * mm, "end": v(7.14, -30.39) * mm});
            skLineSegment(sketch, "E229", {"start": v(7.14, -30.39) * mm, "end": v(11.79, -28.17) * mm});
            skLineSegment(sketch, "E230", {"start": v(11.79, -28.17) * mm, "end": v(0, -7.4) * mm});
            skLineSegment(sketch, "E231", {"start": v(12.69, -38.23) * mm, "end": v(0, -49.53) * mm});
            skLineSegment(sketch, "E232.MirrorCS", {"start": v(-15.81, -37.08) * mm, "end": v(-12.68, -32.89) * mm});
            skLineSegment(sketch, "E233.MirrorCS", {"start": v(-9.7, -34.3) * mm, "end": v(-12.69, -38.23) * mm});
            skLineSegment(sketch, "E234.MirrorCS", {"start": v(-12.68, -32.89) * mm, "end": v(-9.7, -34.3) * mm});
            skLineSegment(sketch, "E235.MirrorCS", {"start": v(-15.61, -28.48) * mm, "end": v(-14.1, -26.47) * mm});
            skLineSegment(sketch, "E236.MirrorCS", {"start": v(-8.77, -34.08) * mm, "end": v(-12.86, -32.13) * mm});
            skLineSegment(sketch, "E237.MirrorCS", {"start": v(-15.42, -29.23) * mm, "end": v(-13.18, -26.23) * mm});
            skLineSegment(sketch, "E238.MirrorCS", {"start": v(-11.87, -38.15) * mm, "end": v(-8.77, -34.08) * mm});
            skLineSegment(sketch, "E239.MirrorCS", {"start": v(-12.86, -32.13) * mm, "end": v(-16, -36.32) * mm});
            skLineSegment(sketch, "E240.MirrorCS", {"start": v(-7.36, -29.62) * mm, "end": v(-10.95, -27.9) * mm});
            skLineSegment(sketch, "E241.MirrorCS", {"start": v(-7.14, -30.39) * mm, "end": v(-11.79, -28.17) * mm});
            skLineSegment(sketch, "E242.MirrorCS", {"start": v(-60.1, 4) * mm, "end": v(-48.52, 18.4) * mm});
            skLineSegment(sketch, "E243.MirrorCS", {"start": v(-48.52, 50.9) * mm, "end": v(-7.9, 57.48) * mm});
            skLineSegment(sketch, "E244.MirrorCS", {"start": v(-47.92, 18.18) * mm, "end": v(-47.92, 50.38) * mm});
            skLineSegment(sketch, "E245.MirrorCS", {"start": v(-12.69, -38.23) * mm, "end": v(0, -49.53) * mm});
            skLineSegment(sketch, "E246.MirrorCS", {"start": v(-7.36, -29.62) * mm, "end": v(-7.36, -29.62) * mm});
            skLineSegment(sketch, "E247.MirrorCS", {"start": v(0, -18.24) * mm, "end": v(-7.36, -29.62) * mm});
            skLineSegment(sketch, "E248.MirrorCS", {"start": v(-11.79, -28.17) * mm, "end": v(0, -7.4) * mm});
            skLineSegment(sketch, "E249.MirrorCS", {"start": v(-13.18, -26.23) * mm, "end": v(-60.6, -4.63) * mm});
            skLineSegment(sketch, "E250.MirrorCS", {"start": v(0, -48.73) * mm, "end": v(-11.87, -38.15) * mm});
            skLineSegment(sketch, "E251.MirrorCS", {"start": v(-7.9, 57.48) * mm, "end": v(0, 45.69) * mm});
            skLineSegment(sketch, "E252.MirrorCS", {"start": v(-10.95, -27.9) * mm, "end": v(0, -8.6) * mm});
            skLineSegment(sketch, "E253.MirrorCS", {"start": v(-14.1, -26.47) * mm, "end": v(-61.26, -5) * mm});
            skLineSegment(sketch, "E254.MirrorCS", {"start": v(-15.61, -28.48) * mm, "end": v(-67.36, -4.9) * mm});
            skLineSegment(sketch, "E255.MirrorCS", {"start": v(-60.6, -4.63) * mm, "end": v(-59.54, 3.75) * mm});
            skLineSegment(sketch, "E256.MirrorCS", {"start": v(-16, -36.32) * mm, "end": v(-66.16, -12.34) * mm});
            skLineSegment(sketch, "E257.MirrorCS", {"start": v(-48.52, 18.4) * mm, "end": v(-48.52, 50.9) * mm});
            skLineSegment(sketch, "E258.MirrorCS", {"start": v(-59.54, 3.75) * mm, "end": v(-47.92, 18.18) * mm});
            skLineSegment(sketch, "E259.MirrorCS", {"start": v(-67.36, -12.43) * mm, "end": v(-15.81, -37.08) * mm});
            skLineSegment(sketch, "E260.MirrorCS", {"start": v(-47.92, 50.38) * mm, "end": v(-8.18, 56.83) * mm});
            skLineSegment(sketch, "E261.MirrorCS", {"start": v(-67.36, -4.9) * mm, "end": v(-67.36, -12.43) * mm});
            skLineSegment(sketch, "E262.MirrorCS", {"start": v(-8.18, 56.83) * mm, "end": v(0, 44.6) * mm});
            skLineSegment(sketch, "E263.MirrorCS", {"start": v(-66.16, -6.11) * mm, "end": v(-15.42, -29.23) * mm});
            skLineSegment(sketch, "E264.MirrorCS", {"start": v(-66.16, -12.34) * mm, "end": v(-66.16, -6.11) * mm});
            skLineSegment(sketch, "E265.MirrorCS", {"start": v(-61.26, -5) * mm, "end": v(-60.1, 4) * mm});
            skLineSegment(sketch, "E266.MirrorCS", {"start": v(0, -19.35) * mm, "end": v(-7.14, -30.39) * mm});
            skLineSegment(sketch, "E267.MirrorCS", {"start": v(-12.69, -38.23) * mm, "end": v(-12.69, -38.23) * mm});
            skLineSegment(sketch, "E268", {"start": v(0, -7.4) * mm, "end": v(0, 0) * mm});
            skSolve(sketch);
        }
        {
            var Q0;
            Q0 = qSketchRegion(id + "F28", true);
            extrude(context, id + "F29", {"entities" : qUnion([Q0]), "operationType" : NewBodyOperationType.ADD, "depth" : 1 * mm, "offsetDistance" : 25 * mm});
        }
        {
            var Q0;
            Q0=makeQuery(id+"F15.opExtrude","CAP_FACE",FACE,{"disambiguationData":[OSD([sQuery(id+"F14.wireOp",EDGE,"E110"),sQuery(id+"F14.wireOp",EDGE,"E111"),sQuery(id+"F14.wireOp",EDGE,"E112"),sQuery(id+"F14.wireOp",EDGE,"E113"),sQuery(id+"F14.wireOp",EDGE,"E114"),sQuery(id+"F14.wireOp",EDGE,"E115"),sQuery(id+"F14.wireOp",EDGE,"E116"),sQuery(id+"F14.wireOp",EDGE,"E117"),sQuery(id+"F14.wireOp",EDGE,"E118"),sQuery(id+"F14.wireOp",EDGE,"E119"),sQuery(id+"F14.wireOp",EDGE,"E120"),sQuery(id+"F14.wireOp",EDGE,"E121"),sQuery(id+"F14.wireOp",EDGE,"E122"),sQuery(id+"F14.wireOp",EDGE,"E123"),sQuery(id+"F14.wireOp",EDGE,"E124"),sQuery(id+"F14.wireOp",EDGE,"E125"),sQuery(id+"F14.wireOp",EDGE,"E126"),sQuery(id+"F14.wireOp",EDGE,"E127.MirrorCS"),sQuery(id+"F14.wireOp",EDGE,"E128.MirrorCS"),sQuery(id+"F14.wireOp",EDGE,"E129.MirrorCS"),sQuery(id+"F14.wireOp",EDGE,"E130.MirrorCS"),sQuery(id+"F14.wireOp",EDGE,"E131.MirrorCS"),sQuery(id+"F14.wireOp",EDGE,"E132.MirrorCS"),sQuery(id+"F14.wireOp",EDGE,"E133.MirrorCS"),sQuery(id+"F14.wireOp",EDGE,"E134.MirrorCS"),sQuery(id+"F14.wireOp",EDGE,"E135.MirrorCS"),sQuery(id+"F14.wireOp",EDGE,"E136.MirrorCS"),sQuery(id+"F14.wireOp",EDGE,"E137.MirrorCS"),sQuery(id+"F14.wireOp",EDGE,"E138.MirrorCS"),sQuery(id+"F14.wireOp",EDGE,"E139.MirrorCS"),sQuery(id+"F14.wireOp",EDGE,"E140.MirrorCS"),sQuery(id+"F14.wireOp",EDGE,"E141.MirrorCS"),sQuery(id+"F14.wireOp",EDGE,"E142.MirrorCS"),sQuery(id+"F14.wireOp",EDGE,"E143.MirrorCS")])],"isStart":false});
            var sketch = newSketch(context, id + "F30", { "sketchPlane" : qUnion([Q0])});
            skLineSegment(sketch, "E269", {"start": v(0, -18.24) * mm, "end": v(7.36, -29.62) * mm});
            skLineSegment(sketch, "E270", {"start": v(17.03, -0.1) * mm, "end": v(17.03, -0.1) * mm});
            skLineSegment(sketch, "E271", {"start": v(7.36, -29.62) * mm, "end": v(10.95, -27.9) * mm});
            skLineSegment(sketch, "E272", {"start": v(10.95, -27.9) * mm, "end": v(0, -8.6) * mm});
            skLineSegment(sketch, "E273", {"start": v(0, -19.35) * mm, "end": v(7.14, -30.39) * mm});
            skLineSegment(sketch, "E274", {"start": v(7.14, -30.39) * mm, "end": v(11.79, -28.17) * mm});
            skLineSegment(sketch, "E275", {"start": v(11.79, -28.17) * mm, "end": v(0, -7.4) * mm});
            skLineSegment(sketch, "E276", {"start": v(0, -7.4) * mm, "end": v(0, 0) * mm});
            skLineSegment(sketch, "E277.MirrorCS", {"start": v(-11.79, -28.17) * mm, "end": v(0, -7.4) * mm});
            skLineSegment(sketch, "E278.MirrorCS", {"start": v(-10.95, -27.9) * mm, "end": v(0, -8.6) * mm});
            skLineSegment(sketch, "E279.MirrorCS", {"start": v(-7.14, -30.39) * mm, "end": v(-11.79, -28.17) * mm});
            skLineSegment(sketch, "E280.MirrorCS", {"start": v(-7.36, -29.62) * mm, "end": v(-10.95, -27.9) * mm});
            skLineSegment(sketch, "E281.MirrorCS", {"start": v(0, -19.35) * mm, "end": v(-7.14, -30.39) * mm});
            skLineSegment(sketch, "E282.MirrorCS", {"start": v(0, -18.24) * mm, "end": v(-7.36, -29.62) * mm});
            skSolve(sketch);
        }
        {
            var Q0;
            Q0 = qSketchRegion(id + "F30", true);
            extrude(context, id + "F31", {"entities" : qUnion([Q0]), "operationType" : NewBodyOperationType.ADD, "depth" : 1 * mm, "offsetDistance" : 25 * mm});
        }
        {
            var Q0;
            Q0=makeQuery(id+"F29.opExtrude","CAP_FACE",FACE,{"disambiguationData":[OSD([sQuery(id+"F28.wireOp",EDGE,"E198"),sQuery(id+"F28.wireOp",EDGE,"E199"),sQuery(id+"F28.wireOp",EDGE,"E200"),sQuery(id+"F28.wireOp",EDGE,"E201"),sQuery(id+"F28.wireOp",EDGE,"E202"),sQuery(id+"F28.wireOp",EDGE,"E203"),sQuery(id+"F28.wireOp",EDGE,"E205"),sQuery(id+"F28.wireOp",EDGE,"E206"),sQuery(id+"F28.wireOp",EDGE,"E207"),sQuery(id+"F28.wireOp",EDGE,"E208"),sQuery(id+"F28.wireOp",EDGE,"E209"),sQuery(id+"F28.wireOp",EDGE,"E210"),sQuery(id+"F28.wireOp",EDGE,"E211"),sQuery(id+"F28.wireOp",EDGE,"E214"),sQuery(id+"F28.wireOp",EDGE,"E215"),sQuery(id+"F28.wireOp",EDGE,"E216"),sQuery(id+"F28.wireOp",EDGE,"E217"),sQuery(id+"F28.wireOp",EDGE,"E218"),sQuery(id+"F28.wireOp",EDGE,"E219"),sQuery(id+"F28.wireOp",EDGE,"E220"),sQuery(id+"F28.wireOp",EDGE,"E221"),sQuery(id+"F28.wireOp",EDGE,"E222"),sQuery(id+"F28.wireOp",EDGE,"E223"),sQuery(id+"F28.wireOp",EDGE,"E224"),sQuery(id+"F28.wireOp",EDGE,"E225"),sQuery(id+"F28.wireOp",EDGE,"E226"),sQuery(id+"F28.wireOp",EDGE,"E227"),sQuery(id+"F28.wireOp",EDGE,"E231"),sQuery(id+"F28.wireOp",EDGE,"E232.MirrorCS"),sQuery(id+"F28.wireOp",EDGE,"E233.MirrorCS"),sQuery(id+"F28.wireOp",EDGE,"E234.MirrorCS"),sQuery(id+"F28.wireOp",EDGE,"E235.MirrorCS"),sQuery(id+"F28.wireOp",EDGE,"E236.MirrorCS"),sQuery(id+"F28.wireOp",EDGE,"E237.MirrorCS"),sQuery(id+"F28.wireOp",EDGE,"E238.MirrorCS"),sQuery(id+"F28.wireOp",EDGE,"E239.MirrorCS"),sQuery(id+"F28.wireOp",EDGE,"E242.MirrorCS"),sQuery(id+"F28.wireOp",EDGE,"E243.MirrorCS"),sQuery(id+"F28.wireOp",EDGE,"E244.MirrorCS"),sQuery(id+"F28.wireOp",EDGE,"E245.MirrorCS"),sQuery(id+"F28.wireOp",EDGE,"E249.MirrorCS"),sQuery(id+"F28.wireOp",EDGE,"E250.MirrorCS"),sQuery(id+"F28.wireOp",EDGE,"E251.MirrorCS"),sQuery(id+"F28.wireOp",EDGE,"E253.MirrorCS"),sQuery(id+"F28.wireOp",EDGE,"E254.MirrorCS"),sQuery(id+"F28.wireOp",EDGE,"E255.MirrorCS"),sQuery(id+"F28.wireOp",EDGE,"E256.MirrorCS"),sQuery(id+"F28.wireOp",EDGE,"E257.MirrorCS"),sQuery(id+"F28.wireOp",EDGE,"E258.MirrorCS"),sQuery(id+"F28.wireOp",EDGE,"E259.MirrorCS"),sQuery(id+"F28.wireOp",EDGE,"E260.MirrorCS"),sQuery(id+"F28.wireOp",EDGE,"E261.MirrorCS"),sQuery(id+"F28.wireOp",EDGE,"E262.MirrorCS"),sQuery(id+"F28.wireOp",EDGE,"E263.MirrorCS"),sQuery(id+"F28.wireOp",EDGE,"E264.MirrorCS"),sQuery(id+"F28.wireOp",EDGE,"E265.MirrorCS")])],"isStart":false});
            var sketch = newSketch(context, id + "F32", { "sketchPlane" : qUnion([Q0])});
            skLineSegment(sketch, "E283.bottom", {"start": v(66.16, -6.11) * mm, "end": v(67.36, -6.11) * mm});
            skLineSegment(sketch, "E283.top", {"start": v(66.16, -12.43) * mm, "end": v(67.36, -12.43) * mm});
            skLineSegment(sketch, "E283.left", {"start": v(66.16, -6.11) * mm, "end": v(66.16, -12.43) * mm});
            skLineSegment(sketch, "E283.right", {"start": v(67.36, -6.11) * mm, "end": v(67.36, -12.43) * mm});
            skLineSegment(sketch, "E284.MirrorCS", {"start": v(-66.16, -12.43) * mm, "end": v(-67.36, -12.43) * mm});
            skLineSegment(sketch, "E285.MirrorCS", {"start": v(-66.16, -6.11) * mm, "end": v(-67.36, -6.11) * mm});
            skLineSegment(sketch, "E286.MirrorCS", {"start": v(-67.36, -6.11) * mm, "end": v(-67.36, -12.43) * mm});
            skLineSegment(sketch, "E287.MirrorCS", {"start": v(-66.16, -6.11) * mm, "end": v(-66.16, -12.43) * mm});
            skLineSegment(sketch, "E288", {"start": v(12.69, -38.23) * mm, "end": v(0, -49.53) * mm});
            skLineSegment(sketch, "E289", {"start": v(0, -49.53) * mm, "end": v(0, -48.73) * mm});
            skLineSegment(sketch, "E290", {"start": v(0, -48.73) * mm, "end": v(12.32, -37.75) * mm});
            skLineSegment(sketch, "E291", {"start": v(12.32, -37.75) * mm, "end": v(12.69, -38.23) * mm});
            skLineSegment(sketch, "E292.MirrorCS", {"start": v(-12.32, -37.75) * mm, "end": v(-12.69, -38.23) * mm});
            skLineSegment(sketch, "E293.MirrorCS", {"start": v(0, -48.73) * mm, "end": v(-12.32, -37.75) * mm});
            skLineSegment(sketch, "E294.MirrorCS", {"start": v(-12.69, -38.23) * mm, "end": v(0, -49.53) * mm});
            skSolve(sketch);
        }
        {
            var Q0;
            Q0 = qSketchRegion(id + "F32", true);
            extrude(context, id + "F33", {"entities" : qUnion([Q0]), "operationType" : NewBodyOperationType.ADD, "depth" : 1 * mm, "offsetDistance" : 25 * mm});
        }
        {
            var Q0;
            Q0=makeQuery(id+"F29.opExtrude","CAP_EDGE",EDGE,{"disambiguationData":[OSD([sQuery(id+"F28.wireOp",EDGE,"E222")])],"isStart":false});
            var Q1;
            Q1=makeQuery(id+"F29.opExtrude","CAP_EDGE",EDGE,{"disambiguationData":[OSD([sQuery(id+"F28.wireOp",EDGE,"E214")])],"isStart":false});
            var Q2;
            Q2=makeQuery(id+"F29.opExtrude","CAP_EDGE",EDGE,{"disambiguationData":[OSD([sQuery(id+"F28.wireOp",EDGE,"E211")])],"isStart":false});
            var Q3;
            Q3=makeQuery(id+"F29.opExtrude","CAP_EDGE",EDGE,{"disambiguationData":[OSD([sQuery(id+"F28.wireOp",EDGE,"E200")])],"isStart":false});
            var Q4;
            Q4=makeQuery(id+"F29.opExtrude","CAP_EDGE",EDGE,{"disambiguationData":[OSD([sQuery(id+"F28.wireOp",EDGE,"E201")])],"isStart":false});
            var Q5;
            Q5=makeQuery(id+"F29.opExtrude","CAP_EDGE",EDGE,{"disambiguationData":[OSD([sQuery(id+"F28.wireOp",EDGE,"E202")])],"isStart":false});
            var Q6;
            Q6=makeQuery(id+"F29.opExtrude","CAP_EDGE",EDGE,{"disambiguationData":[OSD([sQuery(id+"F28.wireOp",EDGE,"E203")])],"isStart":false});
            var Q7;
            Q7=makeQuery(id+"F29.opExtrude","CAP_EDGE",EDGE,{"disambiguationData":[OSD([sQuery(id+"F28.wireOp",EDGE,"E223")])],"isStart":false});
            var Q8;
            Q8=makeQuery(id+"F29.opExtrude","CAP_EDGE",EDGE,{"disambiguationData":[OSD([sQuery(id+"F28.wireOp",EDGE,"E225")])],"isStart":false});
            var Q9;
            Q9=makeQuery(id+"F29.opExtrude","CAP_EDGE",EDGE,{"disambiguationData":[OSD([sQuery(id+"F28.wireOp",EDGE,"E205")])],"isStart":false});
            var Q10;
            Q10=makeQuery(id+"F29.opExtrude","CAP_EDGE",EDGE,{"disambiguationData":[OSD([sQuery(id+"F28.wireOp",EDGE,"E250.MirrorCS")])],"isStart":false});
            var Q11;
            Q11=makeQuery(id+"F29.opExtrude","CAP_EDGE",EDGE,{"disambiguationData":[OSD([sQuery(id+"F28.wireOp",EDGE,"E233.MirrorCS")])],"isStart":false});
            var Q12;
            Q12=makeQuery(id+"F29.opExtrude","CAP_EDGE",EDGE,{"disambiguationData":[OSD([sQuery(id+"F28.wireOp",EDGE,"E234.MirrorCS")])],"isStart":false});
            var Q13;
            Q13=makeQuery(id+"F29.opExtrude","CAP_EDGE",EDGE,{"disambiguationData":[OSD([sQuery(id+"F28.wireOp",EDGE,"E232.MirrorCS")])],"isStart":false});
            var Q14;
            Q14=makeQuery(id+"F29.opExtrude","CAP_EDGE",EDGE,{"disambiguationData":[OSD([sQuery(id+"F28.wireOp",EDGE,"E259.MirrorCS")])],"isStart":false});
            var Q15;
            Q15=makeQuery(id+"F29.opExtrude","CAP_EDGE",EDGE,{"disambiguationData":[OSD([sQuery(id+"F28.wireOp",EDGE,"E226")])],"isStart":false});
            var Q16;
            Q16=makeQuery(id+"F29.opExtrude","CAP_EDGE",EDGE,{"disambiguationData":[OSD([sQuery(id+"F28.wireOp",EDGE,"E227")])],"isStart":false});
            var Q17;
            Q17=makeQuery(id+"F29.opExtrude","CAP_EDGE",EDGE,{"disambiguationData":[OSD([sQuery(id+"F28.wireOp",EDGE,"E262.MirrorCS")])],"isStart":false});
            var Q18;
            Q18=makeQuery(id+"F29.opExtrude","CAP_EDGE",EDGE,{"disambiguationData":[OSD([sQuery(id+"F28.wireOp",EDGE,"E260.MirrorCS")])],"isStart":false});
            var Q19;
            Q19=makeQuery(id+"F29.opExtrude","CAP_EDGE",EDGE,{"disambiguationData":[OSD([sQuery(id+"F28.wireOp",EDGE,"E244.MirrorCS")])],"isStart":false});
            var Q20;
            Q20=makeQuery(id+"F29.opExtrude","CAP_EDGE",EDGE,{"disambiguationData":[OSD([sQuery(id+"F28.wireOp",EDGE,"E258.MirrorCS")])],"isStart":false});
            var Q21;
            Q21=makeQuery(id+"F29.opExtrude","CAP_EDGE",EDGE,{"disambiguationData":[OSD([sQuery(id+"F28.wireOp",EDGE,"E255.MirrorCS")])],"isStart":false});
            var Q22;
            Q22=makeQuery(id+"F29.opExtrude","CAP_EDGE",EDGE,{"disambiguationData":[OSD([sQuery(id+"F28.wireOp",EDGE,"E249.MirrorCS")])],"isStart":false});
            var Q23;
            Q23=makeQuery(id+"F29.opExtrude","CAP_EDGE",EDGE,{"disambiguationData":[OSD([sQuery(id+"F28.wireOp",EDGE,"E263.MirrorCS")])],"isStart":false});
            var Q24;
            Q24=makeQuery(id+"F29.opExtrude","CAP_EDGE",EDGE,{"disambiguationData":[OSD([sQuery(id+"F28.wireOp",EDGE,"E237.MirrorCS")])],"isStart":false});
            var Q25;
            Q25=makeQuery(id+"F31.opExtrude","CAP_EDGE",EDGE,{"disambiguationData":[OSD([sQuery(id+"F30.wireOp",EDGE,"E275")])],"isStart":false});
            var Q26;
            Q26=makeQuery(id+"F31.opExtrude","CAP_EDGE",EDGE,{"disambiguationData":[OSD([sQuery(id+"F30.wireOp",EDGE,"E274")])],"isStart":false});
            var Q27;
            Q27=makeQuery(id+"F31.opExtrude","CAP_EDGE",EDGE,{"disambiguationData":[OSD([sQuery(id+"F30.wireOp",EDGE,"E273")])],"isStart":false});
            var Q28;
            Q28=makeQuery(id+"F31.opExtrude","CAP_EDGE",EDGE,{"disambiguationData":[OSD([sQuery(id+"F30.wireOp",EDGE,"E281.MirrorCS")])],"isStart":false});
            var Q29;
            Q29=makeQuery(id+"F31.opExtrude","CAP_EDGE",EDGE,{"disambiguationData":[OSD([sQuery(id+"F30.wireOp",EDGE,"E279.MirrorCS")])],"isStart":false});
            var Q30;
            Q30=makeQuery(id+"F31.opExtrude","CAP_EDGE",EDGE,{"disambiguationData":[OSD([sQuery(id+"F30.wireOp",EDGE,"E277.MirrorCS")])],"isStart":false});
            var Q31;
            Q31=makeQuery(id+"F29.opExtrude","CAP_EDGE",EDGE,{"disambiguationData":[OSD([sQuery(id+"F28.wireOp",EDGE,"E224")])],"isStart":false});
            chamfer(context, id + "F34", {"entities" : qUnion([Q0, Q1, Q2, Q3, Q4, Q5, Q6, Q7, Q8, Q9, Q10, Q11, Q12, Q13, Q14, Q15, Q16, Q17, Q18, Q19, Q20, Q21, Q22, Q23, Q24, Q25, Q26, Q27, Q28, Q29, Q30, Q31]), "width" : .4 * mm, "tangentPropagation" : true});
        }
    });
